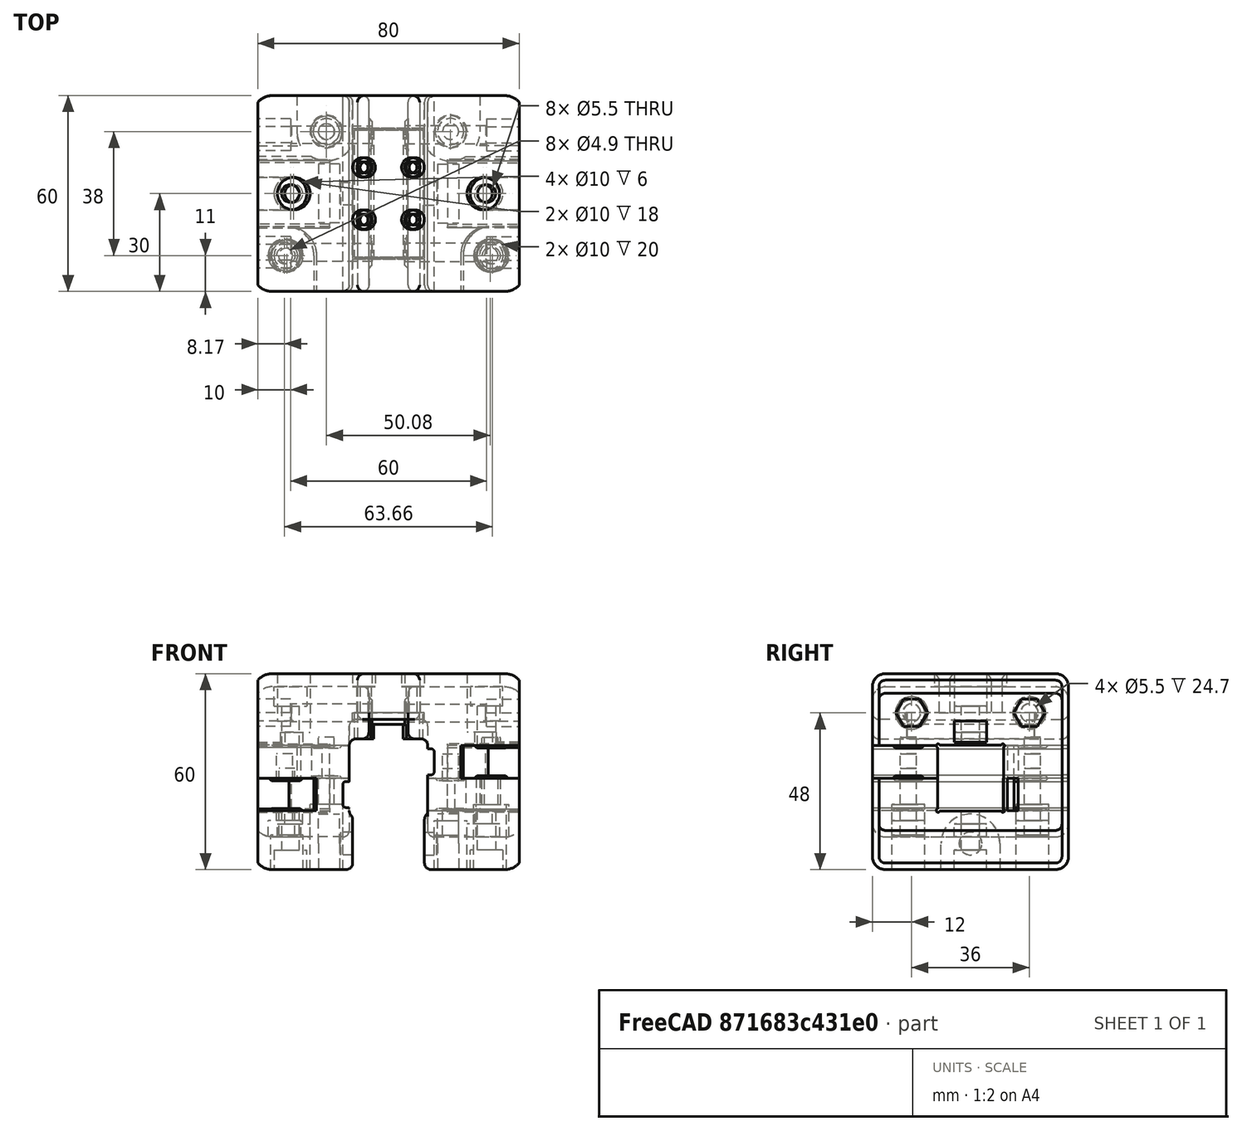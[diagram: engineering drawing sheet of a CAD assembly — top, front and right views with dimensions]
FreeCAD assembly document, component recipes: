
FREECAD ASSEMBLY — COMPONENT RECIPES ("y-carriages")

This assembly document has 7 components, labeled P0..P6 below (a component is one placed body or linked part). 7 of them carry a construction recipe — the FreeCAD feature program that regenerates the part from scratch, quoted from this document or its linked companion documents; the rest are supplied as boundary geometry only. No exploded tour is included for this assembly.
COMPONENT P0 — recipe-attached ("y-carriage-rail-drv", modeled in this document).
Construction recipe (the document's own serialized feature program — sketch geometry with constraints, then the solid features built on it; lengths are millimeters unless a unit is written):

FEATURE [Sketcher::SketchObject] Sketch
  ArcFitTolerance = 1e-06
  AttachmentSupport = -> [YZ_Plane257]
  FullyConstrained = true
  MakeInternals = false
  MapMode = 5
  Placement = pos=(0,0,0) rot=(0.57735,0.57735,0.57735;2.0944rad)
  sketch-geometry (18):
    g0: LineSegment StartX=-30 StartY=28 StartZ=0 EndX=-30 EndY=-14 EndZ=0
    g1: LineSegment StartX=-26 StartY=-18 StartZ=0 EndX=26 EndY=-18 EndZ=0
    g2: LineSegment StartX=30 StartY=-14 StartZ=0 EndX=30 EndY=28 EndZ=0
    g3: LineSegment StartX=26 StartY=32 StartZ=0 EndX=-26 EndY=32 EndZ=0
    g4: ArcOfCircle CenterX=26 CenterY=28 CenterZ=0 NormalX=0 NormalY=0 NormalZ=1 AngleXU=0 Radius=4 StartAngle=0 EndAngle=1.5708
    g5: GeomPoint [constr] X=30 Y=32 Z=0
    g6: ArcOfCircle CenterX=26 CenterY=-14 CenterZ=0 NormalX=0 NormalY=0 NormalZ=1 AngleXU=0 Radius=4 StartAngle=4.71239 EndAngle=6.28319
    g7: GeomPoint [constr] X=30 Y=-18 Z=0
    g8: ArcOfCircle CenterX=-26 CenterY=-14 CenterZ=0 NormalX=0 NormalY=0 NormalZ=1 AngleXU=0 Radius=4 StartAngle=3.14159 EndAngle=4.71239
    g9: GeomPoint [constr] X=-30 Y=-18 Z=0
    g10: ArcOfCircle CenterX=-26 CenterY=28 CenterZ=0 NormalX=0 NormalY=0 NormalZ=1 AngleXU=0 Radius=4 StartAngle=1.5708 EndAngle=3.14159
    g11: GeomPoint [constr] X=-30 Y=32 Z=0
    g12: LineSegment [constr] StartX=-10 StartY=10 StartZ=0 EndX=-10 EndY=-10 EndZ=0
    g13: LineSegment [constr] StartX=-10 StartY=-10 StartZ=0 EndX=10 EndY=-10 EndZ=0
    g14: LineSegment [constr] StartX=10 StartY=-10 StartZ=0 EndX=10 EndY=10 EndZ=0
    g15: LineSegment [constr] StartX=10 StartY=10 StartZ=0 EndX=-10 EndY=10 EndZ=0
    g16: GeomPoint [constr] X=0 Y=20 Z=0
    g17: GeomPoint [constr] X=0 Y=32 Z=0
  constraints (42):
    c: Vertical(g0)
    c: Vertical(g2)
    c: Horizontal(g1)
    c: Symmetric(g5,g11,g-2)
    c: PointOnObject(g5,g2)
    c: PointOnObject(g5,g3)
    c: Tangent(g2,g4) = -1.5708
    c: Tangent(g3,g4) = -1.5708
    c: PointOnObject(g7,g1)
    c: PointOnObject(g7,g2)
    c: Tangent(g1,g6) = -1.5708
    c: Tangent(g2,g6) = -1.5708
    c: PointOnObject(g9,g0)
    c: PointOnObject(g9,g1)
    c: Tangent(g0,g8) = -1.5708
    c: Tangent(g1,g8) = -1.5708
    c: PointOnObject(g11,g0)
    c: PointOnObject(g11,g3)
    c: Tangent(g0,g10) = -1.5708
    c: Tangent(g3,g10) = -1.5708
    c: Equal(g10,g4)
    c: Equal(g4,g6)
    c: Equal(g6,g8)
    c: Radius(g8) = 4
    c: Coincident(g12,g13)
    c: Coincident(g13,g14)
    c: Coincident(g14,g15)
    c: Coincident(g15,g12)
    c: Vertical(g12)
    c: Vertical(g14)
    c: Horizontal(g13)
    c: Horizontal(g15)
    c: Symmetric(g13,g12,g-1)
    c: Equal(g14,g15)
    c: DistanceX(g15,g15) = 20
    c: DistanceY(g7,g13) = 8
    c: DistanceX(g11,g5) = 60
    c: PointOnObject(g16,g-2)
    c: DistanceY(g16) = 20
    c: PointOnObject(g17,g3)
    c: PointOnObject(g17,g-2)
    c: DistanceY(g16,g17) = 12
FEATURE [PartDesign::Pad] Pad
  Direction = (1,0,0)
  Length = 40
  Length2 = 9.5
  Placement = pos=(0,0,0) rot=(1,1,1;2.0944rad)
  Profile = -> Sketch
  ReferenceAxis = -> Sketch [N_Axis]
  Suppressed = false
  Type = 4
FEATURE [Sketcher::SketchObject] Sketch469
  ArcFitTolerance = 0
  AttachmentOffset = pos=(0,0,18) rot=(0,0,1;0rad)
  AttachmentSupport = -> [YZ_Plane257]
  FullyConstrained = true
  MakeInternals = false
  MapMode = 5
  Placement = pos=(18,0,0) rot=(0.57735,0.57735,0.57735;2.0944rad)
  sketch-geometry (20):
    g0: LineSegment StartX=-9.4043 StartY=10.1 StartZ=0 EndX=9.4043 EndY=10.1 EndZ=0
    g1: LineSegment StartX=10.1 StartY=9.4043 StartZ=0 EndX=10.1 EndY=-9.4043 EndZ=0
    g2: LineSegment StartX=9.4043 StartY=-10.1 StartZ=0 EndX=-9.4043 EndY=-10.1 EndZ=0
    g3: LineSegment StartX=-10.1 StartY=-9.4043 StartZ=0 EndX=-10.1 EndY=9.4043 EndZ=0
    g4: ArcOfCircle CenterX=-9.92607 CenterY=9.92607 CenterZ=0 NormalX=0 NormalY=0 NormalZ=1 AngleXU=0 Radius=0.55 StartAngle=0.321751 EndAngle=4.39064
    g5: ArcOfCircle CenterX=9.92607 CenterY=9.92607 CenterZ=0 NormalX=0 NormalY=0 NormalZ=1 AngleXU=0 Radius=0.55 StartAngle=5.03414 EndAngle=9.10303
    g6: ArcOfCircle CenterX=9.92607 CenterY=-9.92607 CenterZ=0 NormalX=0 NormalY=0 NormalZ=1 AngleXU=0 Radius=0.55 StartAngle=3.46334 EndAngle=7.53223
    g7: ArcOfCircle CenterX=-9.92607 CenterY=-9.92607 CenterZ=0 NormalX=0 NormalY=0 NormalZ=1 AngleXU=0 Radius=0.55 StartAngle=1.89255 EndAngle=5.96143
    g8: LineSegment [constr] StartX=-10.1 StartY=9.4043 StartZ=0 EndX=-9.4043 EndY=10.1 EndZ=0
    g9: LineSegment [constr] StartX=9.4043 StartY=10.1 StartZ=0 EndX=10.1 EndY=9.4043 EndZ=0
    g10: LineSegment [constr] StartX=9.4043 StartY=-10.1 StartZ=0 EndX=10.1 EndY=-9.4043 EndZ=0
    g11: LineSegment [constr] StartX=-10.1 StartY=-9.4043 StartZ=0 EndX=-9.4043 EndY=-10.1 EndZ=0
    g12: GeomPoint [constr] X=-10.1 Y=10.1 Z=0
    g13: GeomPoint [constr] X=-9.75215 Y=9.75215 Z=0
    g14: GeomPoint [constr] X=9.75215 Y=9.75215 Z=0
    g15: GeomPoint [constr] X=10.1 Y=10.1 Z=0
    g16: GeomPoint [constr] X=-10.1 Y=-10.1 Z=0
    g17: GeomPoint [constr] X=-9.75215 Y=-9.75215 Z=0
    g18: GeomPoint [constr] X=10.1 Y=-10.1 Z=0
    g19: GeomPoint [constr] X=9.75215 Y=-9.75215 Z=0
  constraints (43):
    c: Horizontal(g0)
    c: Horizontal(g2)
    c: Vertical(g1)
    c: Vertical(g3)
    c: Coincident(g0,g4)
    c: Coincident(g3,g4)
    c: Coincident(g1,g5)
    c: Coincident(g0,g5)
    c: Coincident(g2,g6)
    c: Coincident(g1,g6)
    c: Coincident(g2,g7)
    c: Coincident(g3,g7)
    c: Coincident(g8,g3)
    c: Coincident(g8,g0)
    c: Coincident(g9,g0)
    c: Coincident(g9,g1)
    c: Coincident(g10,g2)
    c: Coincident(g10,g1)
    c: Coincident(g11,g3)
    c: Coincident(g11,g2)
    c: Equal(g6,g7)
    c: Equal(g7,g4)
    c: Equal(g4,g5)
    c: Parallel(g8,g10)
    c: Parallel(g11,g9)
    c: Perpendicular(g10,g9)
    c: Angle(g10) = 0.785398
    c: Radius(g4) = 0.55
    c: PointOnObject(g12,g0)
    c: Symmetric(g3,g0,g13)
    c: Symmetric(g13,g12,g4)
    c: Symmetric(g1,g0,g14)
    c: PointOnObject(g15,g1)
    c: Symmetric(g14,g15,g5)
    c: Symmetric(g3,g2,g17)
    c: PointOnObject(g16,g2)
    c: Symmetric(g16,g17,g7)
    c: PointOnObject(g18,g1)
    c: Symmetric(g18,g19,g6)
    c: Symmetric(g2,g1,g19)
    c: Symmetric(g18,g12,g-1)
    c: DistanceX(g16,g18) = 20.2
    c: DistanceY(g16,g12) = 20.2
FEATURE [PartDesign::Pocket] Pocket
  BaseFeature = -> Pad
  Direction = (-1,0,0)
  Length = 5
  Length2 = 5
  Placement = pos=(0,0,0) rot=(1,1,1;2.0944rad)
  Profile = -> Sketch469
  ReferenceAxis = -> Sketch469 [N_Axis]
  Reversed = true
  Suppressed = false
  Type = 1
FEATURE [Sketcher::SketchObject] Sketch470
  ArcFitTolerance = 1e-06
  AttachmentSupport = -> [XZ_Plane257]
  FullyConstrained = true
  MakeInternals = false
  MapMode = 5
  Placement = pos=(0,0,0) rot=(1,0,0;1.5708rad)
  sketch-geometry (10):
    g0: LineSegment [constr] StartX=-10 StartY=10 StartZ=0 EndX=-10 EndY=-10 EndZ=0
    g1: LineSegment [constr] StartX=-10 StartY=-10 StartZ=0 EndX=10 EndY=-10 EndZ=0
    g2: LineSegment [constr] StartX=10 StartY=-10 StartZ=0 EndX=10 EndY=10 EndZ=0
    g3: LineSegment [constr] StartX=10 StartY=10 StartZ=0 EndX=-10 EndY=10 EndZ=0
    g4: LineSegment StartX=-10 StartY=18 StartZ=0 EndX=-10 EndY=-28 EndZ=0
    g5: LineSegment StartX=-10 StartY=-28 StartZ=0 EndX=12 EndY=-28 EndZ=0
    g6: LineSegment StartX=12 StartY=-28 StartZ=0 EndX=12 EndY=16 EndZ=0
    g7: LineSegment StartX=10 StartY=18 StartZ=0 EndX=-10 EndY=18 EndZ=0
    g8: ArcOfCircle CenterX=10 CenterY=16 CenterZ=0 NormalX=0 NormalY=0 NormalZ=1 AngleXU=0 Radius=2 StartAngle=0 EndAngle=1.5708
    g9: GeomPoint [constr] X=12 Y=18 Z=0
  constraints (27):
    c: Coincident(g0,g1)
    c: Coincident(g1,g2)
    c: Coincident(g2,g3)
    c: Coincident(g3,g0)
    c: Vertical(g0)
    c: Vertical(g2)
    c: Horizontal(g1)
    c: Horizontal(g3)
    c: Symmetric(g1,g0,g-1)
    c: Equal(g2,g3)
    c: DistanceX(g3,g3) = 20
    c: Coincident(g4,g5)
    c: Coincident(g5,g6)
    c: Coincident(g7,g4)
    c: Vertical(g4)
    c: Vertical(g6)
    c: Horizontal(g5)
    c: Horizontal(g7)
    c: DistanceX(g2,g9) = 2
    c: PointOnObject(g0,g4)
    c: DistanceY(g5) = -28
    c: DistanceY(g2,g9) = 8
    c: PointOnObject(g9,g6)
    c: PointOnObject(g9,g7)
    c: Tangent(g6,g8) = -1.5708
    c: Tangent(g7,g8) = -1.5708
    c: Radius(g8) = 2
FEATURE [PartDesign::Pocket] Pocket181
  BaseFeature = -> Pocket
  Direction = (0,1,-2e-16)
  Length = 5
  Length2 = 5
  Midplane = true
  Placement = pos=(0,0,0) rot=(1,1,1;2.0944rad)
  Profile = -> Sketch470
  ReferenceAxis = -> Sketch470 [N_Axis]
  Suppressed = false
  Type = 1
FEATURE [Sketcher::SketchObject] Sketch471
  ArcFitTolerance = 1e-06
  AttachmentSupport = -> [XZ_Plane257]
  FullyConstrained = true
  MakeInternals = false
  MapMode = 5
  Placement = pos=(0,0,0) rot=(1,0,0;1.5708rad)
  sketch-geometry (4):
    g0: LineSegment StartX=-11 StartY=20 StartZ=0 EndX=-11 EndY=0 EndZ=0
    g1: LineSegment StartX=-11 StartY=0 StartZ=0 EndX=11 EndY=0 EndZ=0
    g2: LineSegment StartX=11 StartY=0 StartZ=0 EndX=11 EndY=20 EndZ=0
    g3: LineSegment StartX=11 StartY=20 StartZ=0 EndX=-11 EndY=20 EndZ=0
  constraints (11):
    c: Coincident(g0,g1)
    c: Coincident(g1,g2)
    c: Coincident(g2,g3)
    c: Coincident(g3,g0)
    c: Vertical(g0)
    c: Vertical(g2)
    c: Horizontal(g1)
    c: Symmetric(g2,g0,g-2)
    c: DistanceX(g3,g3) = 22
    c: DistanceY(g2) = 20
    c: PointOnObject(g1,g-1)
FEATURE [PartDesign::Pocket] Pocket182
  BaseFeature = -> Pocket181
  Direction = (0,1,-2e-16)
  Length = 40
  Length2 = 5
  Midplane = true
  Placement = pos=(0,0,0) rot=(1,1,1;2.0944rad)
  Profile = -> Sketch471
  ReferenceAxis = -> Sketch471 [N_Axis]
  Suppressed = false
  Type = 0
FEATURE [Sketcher::SketchObject] Sketch472
  ArcFitTolerance = 1e-06
  AttachmentOffset = pos=(8,0,8) rot=(0,0,1;0rad)
  AttachmentSupport = -> [YZ_Plane257]
  FullyConstrained = true
  MakeInternals = false
  MapMode = 5
  Placement = pos=(8,8,0) rot=(0.57735,0.57735,0.57735;2.0944rad)
  sketch-geometry (6):
    g0: LineSegment StartX=0 StartY=32 StartZ=0 EndX=3 EndY=32 EndZ=0
    g1: LineSegment StartX=3 StartY=32 StartZ=0 EndX=3 EndY=28 EndZ=0
    g2: LineSegment StartX=3 StartY=28 StartZ=0 EndX=1.7 EndY=28 EndZ=0
    g3: LineSegment StartX=1.7 StartY=28 StartZ=0 EndX=1.7 EndY=20 EndZ=0
    g4: LineSegment StartX=1.7 StartY=20 StartZ=0 EndX=0 EndY=20 EndZ=0
    g5: LineSegment StartX=0 StartY=20 StartZ=0 EndX=0 EndY=32 EndZ=0
  constraints (18):
    c: PointOnObject(g0,g-2)
    c: Horizontal(g0)
    c: Coincident(g0,g1)
    c: Vertical(g1)
    c: Coincident(g1,g2)
    c: Horizontal(g2)
    c: Coincident(g2,g3)
    c: Vertical(g3)
    c: Coincident(g3,g4)
    c: PointOnObject(g4,g-2)
    c: Horizontal(g4)
    c: Coincident(g4,g5)
    c: Coincident(g5,g0)
    c: DistanceY(g4) = 20
    c: DistanceX(g4,g4) = 1.7
    c: DistanceY(g3,g3) = 8
    c: DistanceX(g0,g0) = 3
    c: DistanceY(g0) = 32
FEATURE [PartDesign::Groove] Groove
  Angle = 360
  Angle2 = 60
  Axis = (0,0,1)
  Base = (8,8,0)
  BaseFeature = -> Pocket182
  Placement = pos=(0,0,0) rot=(1,1,1;2.0944rad)
  Profile = -> Sketch472
  ReferenceAxis = -> Sketch472 [V_Axis]
  Suppressed = false
  Type = 0
FEATURE [PartDesign::LinearPattern] LinearPattern
  Direction = -> X_Axis258
  Length = 15
  Mode = 0
  Occurrences = 2
  Offset = 15
  Placement = pos=(0,0,0) rot=(1,1,1;2.0944rad)
  Reversed = true
  Suppressed = false
  TransformMode = 0
FEATURE [PartDesign::Mirrored] Mirrored
  MirrorPlane = -> XZ_Plane257
  Placement = pos=(0,0,0) rot=(1,1,1;2.0944rad)
  Suppressed = false
  TransformMode = 0
FEATURE [PartDesign::MultiTransform] MultiTransform
  BaseFeature = -> Groove
  Originals = -> [Groove]
  Placement = pos=(0,0,0) rot=(1,1,1;2.0944rad)
  Suppressed = false
  TransformMode = 0
  Transformations = -> [LinearPattern,Mirrored]
FEATURE [Sketcher::SketchObject] Sketch473
  ArcFitTolerance = 1e-06
  AttachmentOffset = pos=(29,0,0) rot=(0,0,1;0rad)
  AttachmentSupport = -> [XZ_Plane257]
  FullyConstrained = true
  MakeInternals = false
  MapMode = 5
  Placement = pos=(29,0,0) rot=(1,0,0;1.5708rad)
  sketch-geometry (6):
    g0: LineSegment StartX=0 StartY=10 StartZ=0 EndX=0 EndY=32 EndZ=0
    g1: LineSegment StartX=0 StartY=32 StartZ=0 EndX=5 EndY=32 EndZ=0
    g2: LineSegment StartX=5 StartY=32 StartZ=0 EndX=5 EndY=14 EndZ=0
    g3: LineSegment StartX=5 StartY=14 StartZ=0 EndX=2.75 EndY=14 EndZ=0
    g4: LineSegment StartX=2.75 StartY=14 StartZ=0 EndX=2.75 EndY=10 EndZ=0
    g5: LineSegment StartX=2.75 StartY=10 StartZ=0 EndX=0 EndY=10 EndZ=0
  constraints (18):
    c: Vertical(g0)
    c: Coincident(g0,g1)
    c: Horizontal(g1)
    c: Coincident(g1,g2)
    c: Vertical(g2)
    c: Coincident(g2,g3)
    c: Horizontal(g3)
    c: Coincident(g3,g4)
    c: Vertical(g4)
    c: Coincident(g4,g5)
    c: Coincident(g5,g0)
    c: Horizontal(g5)
    c: DistanceY(g4,g4) = 4
    c: DistanceX(g1,g1) = 5
    c: DistanceY(g0) = 10
    c: DistanceX(g5,g5) = 2.75
    c: DistanceY(g1) = 32
    c: PointOnObject(g0,g-2)
FEATURE [PartDesign::Groove] Groove011
  Angle = 360
  Angle2 = 60
  Axis = (0,2e-16,1)
  Base = (29,0,0)
  BaseFeature = -> MultiTransform
  Placement = pos=(0,0,0) rot=(1,1,1;2.0944rad)
  Profile = -> Sketch473
  ReferenceAxis = -> Sketch473 [V_Axis]
  Suppressed = false
  Type = 0
FEATURE [PartDesign::Mirrored] Mirrored032
  BaseFeature = -> Groove011
  MirrorPlane = -> XY_Plane257
  Originals = -> [Groove011]
  Placement = pos=(0,0,0) rot=(1,1,1;2.0944rad)
  Suppressed = false
  TransformMode = 0
FEATURE [PartDesign::Chamfer] Chamfer
  Angle = 45
  Base = -> Mirrored032 [Edge40]
  BaseFeature = -> Mirrored032
  ChamferType = 0
  FlipDirection = false
  Placement = pos=(0,0,0) rot=(1,1,1;2.0944rad)
  Size = 2
  Size2 = 1
  SupportTransform = false
  Suppressed = false
  UseAllEdges = false
FEATURE [PartDesign::Fillet] Fillet002
  Base = -> Chamfer [Edge70]
  BaseFeature = -> Chamfer
  Placement = pos=(0,0,0) rot=(1,1,1;2.0944rad)
  Radius = 6
  SupportTransform = false
  Suppressed = false
  UseAllEdges = false
FEATURE [PartDesign::Fillet] Fillet003
  Base = -> Fillet002 [Edge3,Edge6,Edge33,Edge29,Edge28,Edge38]
  BaseFeature = -> Fillet002
  Placement = pos=(0,0,0) rot=(1,1,1;2.0944rad)
  Radius = 2
  SupportTransform = false
  Suppressed = false
  UseAllEdges = false
FEATURE [Sketcher::SketchObject] Sketch488
  ArcFitTolerance = 1e-06
  AttachmentSupport = -> [XZ_Plane257]
  FullyConstrained = true
  MakeInternals = false
  MapMode = 5
  Placement = pos=(0,0,0) rot=(1,0,0;1.5708rad)
  sketch-geometry (6):
    g0: LineSegment StartX=40 StartY=11 StartZ=0 EndX=33 EndY=11 EndZ=0
    g1: LineSegment StartX=33 StartY=11 StartZ=0 EndX=33 EndY=14 EndZ=0
    g2: LineSegment StartX=33 StartY=14 StartZ=0 EndX=29 EndY=14 EndZ=0
    g3: LineSegment StartX=29 StartY=14 StartZ=0 EndX=29 EndY=17.5 EndZ=0
    g4: LineSegment StartX=29 StartY=17.5 StartZ=0 EndX=40 EndY=17.5 EndZ=0
    g5: LineSegment StartX=40 StartY=17.5 StartZ=0 EndX=40 EndY=11 EndZ=0
  constraints (18):
    c: Horizontal(g0)
    c: Coincident(g0,g1)
    c: Vertical(g1)
    c: Coincident(g1,g2)
    c: Horizontal(g2)
    c: Coincident(g2,g3)
    c: Vertical(g3)
    c: Coincident(g3,g4)
    c: Horizontal(g4)
    c: Coincident(g4,g5)
    c: Coincident(g5,g0)
    c: Vertical(g5)
    c: DistanceX(g4) = 40
    c: DistanceY(g0) = 11
    c: DistanceY(g5,g5) = 6.5
    c: DistanceX(g0,g0) = 7
    c: DistanceY(g1,g1) = 3
    c: DistanceX(g2) = 29
FEATURE [PartDesign::Pocket] Pocket189
  BaseFeature = -> Fillet003
  Direction = (0,1,-2e-16)
  Length = 10
  Length2 = 5
  Midplane = true
  Placement = pos=(0,0,0) rot=(1,1,1;2.0944rad)
  Profile = -> Sketch488
  ReferenceAxis = -> Sketch488 [N_Axis]
  Refine = true
  Suppressed = false
  Type = 0
FEATURE [PartDesign::Body] Body  label="y-carriage-rail-drv"
  AllowCompound = false
  Group = -> [Sketch,Pad,Sketch469,Pocket,Sketch470,Pocket181,Sketch471,Pocket182,Sketch472,Groove,MultiTransform,LinearPattern,Mirrored,Sketch473,Groove011,Mirrored032,Chamfer,Fillet002,Fillet003,Sketch488,Pocket189]
  Origin = -> Origin258
  Tip = -> Pocket189
COMPONENT P1 — recipe-attached ("y-carriage-vslot-drv", modeled in this document).
Construction recipe (the document's own serialized feature program — sketch geometry with constraints, then the solid features built on it; lengths are millimeters unless a unit is written):

FEATURE [Sketcher::SketchObject] Sketch014
  ArcFitTolerance = 0
  AttachmentOffset = pos=(0,0,15) rot=(0,0,1;0rad)
  AttachmentSupport = -> [YZ_Plane251]
  FullyConstrained = true
  MakeInternals = false
  MapMode = 5
  Placement = pos=(15,0,0) rot=(0.57735,0.57735,0.57735;2.0944rad)
  sketch-geometry (5):
    g0: LineSegment StartX=9 StartY=-20 StartZ=0 EndX=9 EndY=-28 EndZ=0
    g1: LineSegment StartX=9 StartY=-28 StartZ=0 EndX=-9 EndY=-28 EndZ=0
    g2: LineSegment StartX=-9 StartY=-28 StartZ=0 EndX=-9 EndY=-20 EndZ=0
    g3: Circle [constr] CenterX=-5e-16 CenterY=-20 CenterZ=0 NormalX=0 NormalY=0 NormalZ=1 AngleXU=0 Radius=9
    g4: ArcOfCircle CenterX=-5e-16 CenterY=-20 CenterZ=0 NormalX=0 NormalY=0 NormalZ=1 AngleXU=0 Radius=9 StartAngle=0 EndAngle=3.14159
  constraints (12):
    c: Coincident(g0,g1)
    c: Coincident(g1,g2)
    c: Vertical(g0)
    c: Vertical(g2)
    c: Symmetric(g0,g1,g-2)
    c: DistanceY(g0) = -28
    c: DistanceX(g1,g1) = 18
    c: Diameter(g3) = 18
    c: DistanceY(g3) = -20
    c: Tangent(g0,g4) = 1.5708
    c: Tangent(g4,g2) = 1.5708
    c: Coincident(g4,g3)
FEATURE [Sketcher::SketchObject] Sketch015
  ArcFitTolerance = 0
  AttachmentOffset = pos=(0,0,14.7) rot=(0,0,1;0rad)
  AttachmentSupport = -> [YZ_Plane251]
  FullyConstrained = true
  MakeInternals = false
  MapMode = 5
  Placement = pos=(14.7,0,0) rot=(0.57735,0.57735,0.57735;2.0944rad)
  sketch-geometry (1):
    g0: Circle CenterX=0 CenterY=-20 CenterZ=0 NormalX=0 NormalY=0 NormalZ=1 AngleXU=0 Radius=3.5
  constraints (3):
    c: PointOnObject(g0,g-2)
    c: Diameter(g0) = 7
    c: DistanceY(g0) = -20
FEATURE [Sketcher::SketchObject] Sketch016
  ArcFitTolerance = 0
  AttachmentOffset = pos=(0,0,19) rot=(0,0,1;0rad)
  AttachmentSupport = -> [XZ_Plane251]
  FullyConstrained = true
  MakeInternals = false
  MapMode = 5
  Placement = pos=(0,-19,4.2e-15) rot=(1,0,0;1.5708rad)
  sketch-geometry (10):
    g0: GeomPoint [constr] X=31.83 Y=0.25 Z=0
    g1: GeomPoint [constr] X=31.83 Y=5 Z=0
    g2: LineSegment StartX=31.83 StartY=0.25 StartZ=0 EndX=31.83 EndY=0.75 EndZ=0
    g3: LineSegment StartX=31.83 StartY=0.75 StartZ=0 EndX=35.83 EndY=0.75 EndZ=0
    g4: LineSegment StartX=35.83 StartY=0.75 StartZ=0 EndX=36.33 EndY=0.25 EndZ=0
    g5: LineSegment StartX=36.33 StartY=0.25 StartZ=0 EndX=31.83 EndY=0.25 EndZ=0
    g6: LineSegment StartX=31.83 StartY=9.75 StartZ=0 EndX=31.83 EndY=9.25 EndZ=0
    g7: LineSegment StartX=31.83 StartY=9.25 StartZ=0 EndX=35.83 EndY=9.25 EndZ=0
    g8: LineSegment StartX=35.83 StartY=9.25 StartZ=0 EndX=36.33 EndY=9.75 EndZ=0
    g9: LineSegment StartX=36.33 StartY=9.75 StartZ=0 EndX=31.83 EndY=9.75 EndZ=0
  constraints (26):
    c: Vertical(g1,g0)
    c: Coincident(g2,g0)
    c: Vertical(g2)
    c: Coincident(g2,g3)
    c: Horizontal(g3)
    c: Coincident(g3,g4)
    c: Coincident(g4,g5)
    c: Coincident(g5,g2)
    c: Horizontal(g5)
    c: Coincident(g6,g7)
    c: Horizontal(g7)
    c: Coincident(g7,g8)
    c: Coincident(g8,g9)
    c: Coincident(g9,g6)
    c: Vertical(g6)
    c: Horizontal(g9)
    c: Symmetric(g2,g6,g1)
    c: Equal(g2,g6)
    c: DistanceY(g-1,g1) = 5
    c: DistanceX(g1) = 31.83
    c: DistanceY(g2,g6) = 9.5
    c: DistanceY(g2,g2) = 0.5
    c: DistanceX(g3,g3) = 4
    c: Angle(g4) = -0.785398
    c: Perpendicular(g4,g8)
    c: Equal(g9,g5)
FEATURE [Sketcher::SketchObject] Sketch227
  ArcFitTolerance = 0
  AttachmentOffset = pos=(0,0,6) rot=(0,0,1;0rad)
  AttachmentSupport = -> [YZ_Plane251]
  FullyConstrained = true
  MakeInternals = false
  MapMode = 5
  Placement = pos=(6,0,0) rot=(0.57735,0.57735,0.57735;2.0944rad)
  sketch-geometry (12):
    g0: LineSegment StartX=-26 StartY=28 StartZ=0 EndX=26 EndY=28 EndZ=0
    g1: LineSegment StartX=30 StartY=24 StartZ=0 EndX=30 EndY=-24 EndZ=0
    g2: LineSegment StartX=26 StartY=-28 StartZ=0 EndX=-26 EndY=-28 EndZ=0
    g3: LineSegment StartX=-30 StartY=-24 StartZ=0 EndX=-30 EndY=24 EndZ=0
    g4: ArcOfCircle CenterX=-26 CenterY=24 CenterZ=0 NormalX=0 NormalY=0 NormalZ=1 AngleXU=0 Radius=4 StartAngle=1.5708 EndAngle=3.14159
    g5: GeomPoint [constr] X=-30 Y=28 Z=0
    g6: ArcOfCircle CenterX=26 CenterY=24 CenterZ=0 NormalX=0 NormalY=0 NormalZ=1 AngleXU=0 Radius=4 StartAngle=2.62e-14 EndAngle=1.5708
    g7: GeomPoint [constr] X=30 Y=28 Z=0
    g8: ArcOfCircle CenterX=26 CenterY=-24 CenterZ=0 NormalX=0 NormalY=0 NormalZ=1 AngleXU=0 Radius=4 StartAngle=4.71239 EndAngle=6.28319
    g9: GeomPoint [constr] X=30 Y=-28 Z=0
    g10: ArcOfCircle CenterX=-26 CenterY=-24 CenterZ=0 NormalX=0 NormalY=0 NormalZ=1 AngleXU=0 Radius=4 StartAngle=3.14159 EndAngle=4.71239
    g11: GeomPoint [constr] X=-30 Y=-28 Z=0
  constraints (27):
    c: Horizontal(g0)
    c: Horizontal(g2)
    c: Vertical(g1)
    c: Vertical(g3)
    c: Symmetric(g9,g5,g-1)
    c: DistanceY(g9,g7) = 56
    c: DistanceX(g11,g9) = 60
    c: PointOnObject(g5,g0)
    c: PointOnObject(g5,g3)
    c: Tangent(g0,g4) = 1.5708
    c: Tangent(g3,g4) = 1.5708
    c: PointOnObject(g7,g0)
    c: PointOnObject(g7,g1)
    c: Tangent(g0,g6) = 1.5708
    c: Tangent(g1,g6) = 1.5708
    c: PointOnObject(g9,g1)
    c: PointOnObject(g9,g2)
    c: Tangent(g1,g8) = 1.5708
    c: Tangent(g2,g8) = 1.5708
    c: PointOnObject(g11,g2)
    c: PointOnObject(g11,g3)
    c: Tangent(g2,g10) = 1.5708
    c: Tangent(g3,g10) = 1.5708
    c: Equal(g10,g4)
    c: Equal(g4,g6)
    c: Equal(g6,g8)
    c: Radius(g8) = 4
FEATURE [PartDesign::Pad] Pad057
  Direction = (1,0,0)
  Length = 34
  Length2 = 10
  Placement = pos=(0,0,0) rot=(1,1,1;2.0944rad)
  Profile = -> Sketch227
  ReferenceAxis = -> Sketch227 [N_Axis]
  Suppressed = false
  Type = 0
FEATURE [Sketcher::SketchObject] Sketch228
  ArcFitTolerance = 0
  AttachmentOffset = pos=(0,0,18) rot=(0,0,1;0rad)
  AttachmentSupport = -> [YZ_Plane251]
  FullyConstrained = true
  MakeInternals = false
  MapMode = 5
  Placement = pos=(18,0,0) rot=(0.57735,0.57735,0.57735;2.0944rad)
  sketch-geometry (20):
    g0: LineSegment StartX=-9.4043 StartY=10.1 StartZ=0 EndX=9.4043 EndY=10.1 EndZ=0
    g1: LineSegment StartX=10.1 StartY=9.4043 StartZ=0 EndX=10.1 EndY=-9.4043 EndZ=0
    g2: LineSegment StartX=9.4043 StartY=-10.1 StartZ=0 EndX=-9.4043 EndY=-10.1 EndZ=0
    g3: LineSegment StartX=-10.1 StartY=-9.4043 StartZ=0 EndX=-10.1 EndY=9.4043 EndZ=0
    g4: ArcOfCircle CenterX=-9.92607 CenterY=9.92607 CenterZ=0 NormalX=0 NormalY=0 NormalZ=1 AngleXU=0 Radius=0.55 StartAngle=0.321751 EndAngle=4.39064
    g5: ArcOfCircle CenterX=9.92607 CenterY=9.92607 CenterZ=0 NormalX=0 NormalY=0 NormalZ=1 AngleXU=0 Radius=0.55 StartAngle=5.03414 EndAngle=9.10303
    g6: ArcOfCircle CenterX=9.92607 CenterY=-9.92607 CenterZ=0 NormalX=0 NormalY=0 NormalZ=1 AngleXU=0 Radius=0.55 StartAngle=3.46334 EndAngle=7.53223
    g7: ArcOfCircle CenterX=-9.92607 CenterY=-9.92607 CenterZ=0 NormalX=0 NormalY=0 NormalZ=1 AngleXU=0 Radius=0.55 StartAngle=1.89255 EndAngle=5.96143
    g8: LineSegment [constr] StartX=-10.1 StartY=9.4043 StartZ=0 EndX=-9.4043 EndY=10.1 EndZ=0
    g9: LineSegment [constr] StartX=9.4043 StartY=10.1 StartZ=0 EndX=10.1 EndY=9.4043 EndZ=0
    g10: LineSegment [constr] StartX=9.4043 StartY=-10.1 StartZ=0 EndX=10.1 EndY=-9.4043 EndZ=0
    g11: LineSegment [constr] StartX=-10.1 StartY=-9.4043 StartZ=0 EndX=-9.4043 EndY=-10.1 EndZ=0
    g12: GeomPoint [constr] X=-10.1 Y=10.1 Z=0
    g13: GeomPoint [constr] X=-9.75215 Y=9.75215 Z=0
    g14: GeomPoint [constr] X=9.75215 Y=9.75215 Z=0
    g15: GeomPoint [constr] X=10.1 Y=10.1 Z=0
    g16: GeomPoint [constr] X=-10.1 Y=-10.1 Z=0
    g17: GeomPoint [constr] X=-9.75215 Y=-9.75215 Z=0
    g18: GeomPoint [constr] X=10.1 Y=-10.1 Z=0
    g19: GeomPoint [constr] X=9.75215 Y=-9.75215 Z=0
  constraints (43):
    c: Horizontal(g0)
    c: Horizontal(g2)
    c: Vertical(g1)
    c: Vertical(g3)
    c: Coincident(g0,g4)
    c: Coincident(g3,g4)
    c: Coincident(g1,g5)
    c: Coincident(g0,g5)
    c: Coincident(g2,g6)
    c: Coincident(g1,g6)
    c: Coincident(g2,g7)
    c: Coincident(g3,g7)
    c: Coincident(g8,g3)
    c: Coincident(g8,g0)
    c: Coincident(g9,g0)
    c: Coincident(g9,g1)
    c: Coincident(g10,g2)
    c: Coincident(g10,g1)
    c: Coincident(g11,g3)
    c: Coincident(g11,g2)
    c: Equal(g6,g7)
    c: Equal(g7,g4)
    c: Equal(g4,g5)
    c: Parallel(g8,g10)
    c: Parallel(g11,g9)
    c: Perpendicular(g10,g9)
    c: Angle(g10) = 0.785398
    c: Radius(g4) = 0.55
    c: PointOnObject(g12,g0)
    c: Symmetric(g3,g0,g13)
    c: Symmetric(g13,g12,g4)
    c: Symmetric(g1,g0,g14)
    c: PointOnObject(g15,g1)
    c: Symmetric(g14,g15,g5)
    c: Symmetric(g3,g2,g17)
    c: PointOnObject(g16,g2)
    c: Symmetric(g16,g17,g7)
    c: PointOnObject(g18,g1)
    c: Symmetric(g18,g19,g6)
    c: Symmetric(g2,g1,g19)
    c: Symmetric(g18,g12,g-1)
    c: DistanceX(g16,g18) = 20.2
    c: DistanceY(g16,g12) = 20.2
FEATURE [PartDesign::Pocket] Pocket138
  BaseFeature = -> Pad057
  Direction = (-1,0,0)
  Length = 20
  Length2 = 5
  Placement = pos=(0,0,0) rot=(1,1,1;2.0944rad)
  Profile = -> Sketch228
  ReferenceAxis = -> Sketch228 [N_Axis]
  Reversed = true
  Suppressed = false
  Type = 1
FEATURE [Sketcher::SketchObject] Sketch229
  ArcFitTolerance = 0
  AttachmentSupport = -> [XZ_Plane251]
  FullyConstrained = true
  MakeInternals = false
  MapMode = 5
  Placement = pos=(0,0,0) rot=(1,0,0;1.5708rad)
  sketch-geometry (8):
    g0: LineSegment StartX=-10 StartY=12 StartZ=0 EndX=10 EndY=12 EndZ=0
    g1: LineSegment StartX=12 StartY=10 StartZ=0 EndX=12 EndY=-10 EndZ=0
    g2: LineSegment StartX=-12 StartY=-30 StartZ=0 EndX=-12 EndY=10 EndZ=0
    g3: ArcOfCircle CenterX=10 CenterY=10 CenterZ=0 NormalX=0 NormalY=0 NormalZ=1 AngleXU=0 Radius=2 StartAngle=1.8e-15 EndAngle=1.5708
    g4: ArcOfCircle CenterX=10 CenterY=-10 CenterZ=0 NormalX=0 NormalY=0 NormalZ=1 AngleXU=0 Radius=2 StartAngle=5.23599 EndAngle=6.28319
    g5: ArcOfCircle CenterX=-10 CenterY=10 CenterZ=0 NormalX=0 NormalY=0 NormalZ=1 AngleXU=0 Radius=2 StartAngle=1.5708 EndAngle=3.14159
    g6: LineSegment StartX=-12 StartY=-30 StartZ=0 EndX=11 EndY=-30 EndZ=0
    g7: LineSegment StartX=11 StartY=-30 StartZ=0 EndX=11 EndY=-11.7321 EndZ=0
  constraints (21):
    c: Tangent(g0,g3) = 1.5708
    c: Tangent(g1,g3) = 1.5708
    c: Tangent(g1,g4) = 1.5708
    c: Tangent(g0,g5) = 1.5708
    c: Tangent(g2,g5) = 1.5708
    c: Equal(g5,g3)
    c: Equal(g3,g4)
    c: Radius(g3) = 2
    c: DistanceX(g5,g3) = 20
    c: Symmetric(g4,g5,g-1)
    c: Horizontal(g5,g3)
    c: Vertical(g4,g3)
    c: Vertical(g2)
    c: DistanceY(g2) = -30
    c: Coincident(g6,g2)
    c: Horizontal(g6)
    c: Coincident(g7,g6)
    c: Coincident(g7,g4)
    c: Vertical(g7)
    c: DistanceX(g6) = 11
    c: Equal(g1,g0)
FEATURE [PartDesign::Pocket] Pocket139
  BaseFeature = -> Pocket138
  Direction = (0,1,-2e-16)
  Length = 5
  Length2 = 5
  Midplane = true
  Placement = pos=(0,0,0) rot=(1,1,1;2.0944rad)
  Profile = -> Sketch229
  ReferenceAxis = -> Sketch229 [N_Axis]
  Suppressed = false
  Type = 1
FEATURE [Sketcher::SketchObject] Sketch230
  ArcFitTolerance = 0
  AttachmentOffset = pos=(0,0,5) rot=(0,0,1;0rad)
  AttachmentSupport = -> [XY_Plane251]
  FullyConstrained = true
  MakeInternals = false
  MapMode = 5
  Placement = pos=(0,0,5) rot=(0,0,1;0rad)
  sketch-geometry (5):
    g0: ArcOfCircle CenterX=31.83 CenterY=-19 CenterZ=0 NormalX=0 NormalY=0 NormalZ=1 AngleXU=0 Radius=9 StartAngle=1.5708 EndAngle=3.14159
    g1: LineSegment StartX=22.83 StartY=-19 StartZ=0 EndX=22.83 EndY=-30 EndZ=0
    g2: LineSegment StartX=22.83 StartY=-30 StartZ=0 EndX=40.83 EndY=-30 EndZ=0
    g3: LineSegment StartX=40.83 StartY=-30 StartZ=0 EndX=40.83 EndY=-10 EndZ=0
    g4: LineSegment StartX=40.83 StartY=-10 StartZ=0 EndX=31.83 EndY=-10 EndZ=0
  constraints (15):
    c: Diameter(g0) = 18
    c: Vertical(g1)
    c: Coincident(g2,g1)
    c: Horizontal(g2)
    c: Coincident(g3,g2)
    c: Vertical(g3)
    c: Coincident(g4,g3)
    c: Horizontal(g4)
    c: Tangent(g0,g1) = -1.5708
    c: Tangent(g0,g4) = -1.5708
    c: Tangent(g3,g0)
    c: DistanceY(g1) = -30
    c: DistanceX(g0) = 31.83
    c: DistanceY(g0) = -19
    c: DistanceX(g0) = 31.83
FEATURE [Sketcher::SketchObject] Sketch231
  ArcFitTolerance = 0
  AttachmentOffset = pos=(0,0,-5) rot=(0,0,1;0rad)
  AttachmentSupport = -> [XY_Plane251]
  FullyConstrained = true
  MakeInternals = false
  MapMode = 5
  Placement = pos=(0,0,-5) rot=(0,0,1;0rad)
  sketch-geometry (10):
    g0: ArcOfCircle CenterX=19 CenterY=19 CenterZ=0 NormalX=0 NormalY=0 NormalZ=1 AngleXU=0 Radius=9 StartAngle=3.14159 EndAngle=5.25009
    g1: LineSegment StartX=10 StartY=19 StartZ=0 EndX=10 EndY=30 EndZ=0
    g2: LineSegment StartX=10 StartY=30 StartZ=0 EndX=28 EndY=30 EndZ=0
    g3: LineSegment StartX=28 StartY=30 StartZ=0 EndX=28 EndY=19 EndZ=0
    g4: LineSegment StartX=23.6095 StartY=11.27 StartZ=0 EndX=40 EndY=11.27 EndZ=0
    g5: LineSegment StartX=40 StartY=11.27 StartZ=0 EndX=40 EndY=14.65 EndZ=0
    g6: LineSegment StartX=40 StartY=14.65 StartZ=0 EndX=26.8789 EndY=14.65 EndZ=0
    g7: ArcOfCircle CenterX=19 CenterY=19 CenterZ=0 NormalX=0 NormalY=0 NormalZ=1 AngleXU=0 Radius=9 StartAngle=5.77873 EndAngle=6.28319
    g8: GeomPoint [constr] X=19 Y=12.9 Z=0
    g9: Circle [constr] CenterX=19 CenterY=19 CenterZ=0 NormalX=0 NormalY=0 NormalZ=1 AngleXU=0 Radius=6.1
  constraints (27):
    c: Diameter(g0) = 18
    c: Vertical(g1)
    c: Coincident(g2,g1)
    c: Horizontal(g2)
    c: Coincident(g3,g2)
    c: Vertical(g3)
    c: DistanceY(g2) = 30
    c: Tangent(g0,g1) = 1.5708
    c: Horizontal(g4)
    c: Coincident(g5,g4)
    c: Vertical(g5)
    c: Coincident(g6,g5)
    c: Horizontal(g6)
    c: Equal(g0,g7)
    c: Coincident(g0,g4)
    c: Coincident(g7,g6)
    c: Coincident(g0,g7)
    c: Tangent(g7,g3) = 1.5708
    c: DistanceX(g5) = 40
    c: Vertical(g8,g0)
    c: DistanceY(g0,g8) = 1.63
    c: DistanceY(g8,g6) = 1.75
    c: Coincident(g9,g0)
    c: Diameter(g9) = 12.2
    c: PointOnObject(g8,g9)
    c: DistanceX(g0) = 19
    c: DistanceY(g0) = 19
FEATURE [Sketcher::SketchObject] Sketch232
  ArcFitTolerance = 0
  AttachmentOffset = pos=(0,0,29.7) rot=(0,0,1;0rad)
  AttachmentSupport = -> [YZ_Plane251]
  FullyConstrained = true
  MakeInternals = false
  MapMode = 5
  Placement = pos=(29.7,0,0) rot=(0.57735,0.57735,0.57735;2.0944rad)
  sketch-geometry (2):
    g0: Circle CenterX=18 CenterY=20 CenterZ=0 NormalX=0 NormalY=0 NormalZ=1 AngleXU=0 Radius=2.75
    g1: Circle CenterX=-18 CenterY=20 CenterZ=0 NormalX=0 NormalY=0 NormalZ=1 AngleXU=0 Radius=2.75
  constraints (5):
    c: Symmetric(g1,g0,g-2)
    c: Equal(g1,g0)
    c: Diameter(g1) = 5.5
    c: DistanceX(g1,g0) = 36
    c: DistanceY(g0) = 20
FEATURE [Sketcher::SketchObject] Sketch233
  ArcFitTolerance = 0
  AttachmentOffset = pos=(0,0,30) rot=(0,0,1;0rad)
  AttachmentSupport = -> [YZ_Plane251]
  FullyConstrained = true
  MakeInternals = false
  MapMode = 5
  Placement = pos=(30,0,0) rot=(0.57735,0.57735,0.57735;2.0944rad)
  sketch-geometry (14):
    g0: LineSegment StartX=-15.5751 StartY=15.8 StartZ=0 EndX=-13.1503 EndY=20 EndZ=0
    g1: LineSegment StartX=-13.1503 StartY=20 StartZ=0 EndX=-15.5751 EndY=24.2 EndZ=0
    g2: LineSegment StartX=-15.5751 StartY=24.2 StartZ=0 EndX=-20.4249 EndY=24.2 EndZ=0
    g3: LineSegment StartX=-20.4249 StartY=24.2 StartZ=0 EndX=-22.8497 EndY=20 EndZ=0
    g4: LineSegment StartX=-22.8497 StartY=20 StartZ=0 EndX=-20.4249 EndY=15.8 EndZ=0
    g5: LineSegment StartX=-20.4249 StartY=15.8 StartZ=0 EndX=-15.5751 EndY=15.8 EndZ=0
    g6: Circle [constr] CenterX=-18 CenterY=20 CenterZ=0 NormalX=0 NormalY=0 NormalZ=1 AngleXU=0 Radius=4.84974
    g7: LineSegment StartX=20.4249 StartY=15.8 StartZ=0 EndX=22.8497 EndY=20 EndZ=0
    g8: LineSegment StartX=22.8497 StartY=20 StartZ=0 EndX=20.4249 EndY=24.2 EndZ=0
    g9: LineSegment StartX=20.4249 StartY=24.2 StartZ=0 EndX=15.5751 EndY=24.2 EndZ=0
    g10: LineSegment StartX=15.5751 StartY=24.2 StartZ=0 EndX=13.1503 EndY=20 EndZ=0
    g11: LineSegment StartX=13.1503 StartY=20 StartZ=0 EndX=15.5751 EndY=15.8 EndZ=0
    g12: LineSegment StartX=15.5751 StartY=15.8 StartZ=0 EndX=20.4249 EndY=15.8 EndZ=0
    g13: Circle [constr] CenterX=18 CenterY=20 CenterZ=0 NormalX=0 NormalY=0 NormalZ=1 AngleXU=0 Radius=4.84974
  constraints (33):
    c: Coincident(g0,g1)
    c: Coincident(g1,g2)
    c: Coincident(g2,g3)
    c: Coincident(g3,g4)
    c: Coincident(g4,g5)
    c: Coincident(g5,g0)
    c: Equal(g0, g1-g5) x5
    c: PointOnObject(g0,g6)
    c: PointOnObject(g1,g6)
    c: PointOnObject(g2,g6)
    c: PointOnObject(g3,g6)
    c: PointOnObject(g4,g6)
    c: PointOnObject(g5,g6)
    c: Coincident(g7,g8)
    c: Coincident(g8,g9)
    c: Coincident(g9,g10)
    c: Coincident(g10,g11)
    c: Coincident(g11,g12)
    c: Coincident(g12,g7)
    c: Equal(g7, g8-g12) x5
    c: PointOnObject(g7,g13)
    c: PointOnObject(g8,g13)
    c: PointOnObject(g9,g13)
    c: PointOnObject(g10,g13)
    c: PointOnObject(g11,g13)
    c: PointOnObject(g12,g13)
    c: Horizontal(g9)
    c: Horizontal(g2)
    c: Symmetric(g6,g13,g-2)
    c: Equal(g13,g6)
    c: DistanceY(g6) = 20
    c: DistanceX(g6,g13) = 36
    c: DistanceY(g7,g8) = 8.4
FEATURE [Sketcher::SketchObject] Sketch234
  ArcFitTolerance = 0
  AttachmentOffset = pos=(0,0,20) rot=(0,0,1;0rad)
  AttachmentSupport = -> [XY_Plane251]
  FullyConstrained = true
  MakeInternals = false
  MapMode = 5
  Placement = pos=(0,0,20) rot=(0,0,1;0rad)
  sketch-geometry (5):
    g0: GeomPoint [constr] X=6 Y=18 Z=0
    g1: LineSegment StartX=6 StartY=18 StartZ=0 EndX=6 EndY=23 EndZ=0
    g2: LineSegment StartX=6 StartY=23 StartZ=0 EndX=5 EndY=22 EndZ=0
    g3: LineSegment StartX=5 StartY=22 StartZ=0 EndX=5 EndY=18 EndZ=0
    g4: LineSegment StartX=5 StartY=18 StartZ=0 EndX=6 EndY=18 EndZ=0
  constraints (13):
    c: DistanceX(g0) = 6
    c: DistanceY(g0) = 18
    c: Coincident(g1,g0)
    c: Vertical(g1)
    c: Coincident(g1,g2)
    c: Coincident(g2,g3)
    c: Vertical(g3)
    c: Coincident(g3,g4)
    c: Coincident(g4,g1)
    c: Horizontal(g4)
    c: Angle(g2) = -2.35619
    c: DistanceY(g3,g3) = 4
    c: DistanceX(g3) = 5
FEATURE [PartDesign::Revolution] Revolution016
  Angle = 360
  Angle2 = 60
  Axis = (1,0,0)
  Base = (5,18,20)
  BaseFeature = -> Pocket139
  Placement = pos=(0,0,0) rot=(1,1,1;2.0944rad)
  Profile = -> Sketch234
  ReferenceAxis = -> Sketch234 [Edge4]
  Reversed = true
  Suppressed = false
  Type = 0
FEATURE [PartDesign::Mirrored] Mirrored030
  BaseFeature = -> Revolution016
  MirrorPlane = -> XZ_Plane251
  Originals = -> [Revolution016]
  Placement = pos=(0,0,0) rot=(1,1,1;2.0944rad)
  Suppressed = false
  TransformMode = 0
FEATURE [PartDesign::Pocket] Pocket142
  BaseFeature = -> Mirrored030
  Direction = (-1,0,0)
  Length = 5
  Length2 = 5
  Placement = pos=(0,0,0) rot=(1,1,1;2.0944rad)
  Profile = -> Sketch232
  ReferenceAxis = -> Sketch232 [N_Axis]
  Suppressed = false
  Type = 1
FEATURE [PartDesign::Pocket] Pocket143
  BaseFeature = -> Pocket142
  Direction = (-1,0,0)
  Length = 5
  Length2 = 5
  Placement = pos=(0,0,0) rot=(1,1,1;2.0944rad)
  Profile = -> Sketch233
  ReferenceAxis = -> Sketch233 [N_Axis]
  Reversed = true
  Suppressed = false
  Type = 1
FEATURE [Sketcher::SketchObject] Sketch235
  ArcFitTolerance = 0
  AttachmentSupport = -> [XY_Plane251]
  FullyConstrained = true
  MakeInternals = false
  MapMode = 5
  sketch-geometry (1):
    g0: Circle CenterX=30 CenterY=0 CenterZ=0 NormalX=0 NormalY=0 NormalZ=1 AngleXU=0 Radius=2.75
  constraints (3):
    c: PointOnObject(g0,g-1)
    c: DistanceX(g0) = 30
    c: Diameter(g0) = 5.5
FEATURE [PartDesign::Pocket] Pocket144
  BaseFeature = -> Pocket143
  Direction = (0,0,-1)
  Length = 5
  Length2 = 5
  Midplane = true
  Placement = pos=(0,0,0) rot=(1,1,1;2.0944rad)
  Profile = -> Sketch235
  ReferenceAxis = -> Sketch235 [N_Axis]
  Suppressed = false
  Type = 1
FEATURE [Sketcher::SketchObject] Sketch236
  ArcFitTolerance = 0
  AttachmentOffset = pos=(0,0,22) rot=(0,0,1;0rad)
  AttachmentSupport = -> [XY_Plane251]
  FullyConstrained = true
  MakeInternals = false
  MapMode = 5
  Placement = pos=(0,0,22) rot=(0,0,1;0rad)
  sketch-geometry (1):
    g0: Circle CenterX=30 CenterY=0 CenterZ=0 NormalX=0 NormalY=0 NormalZ=1 AngleXU=0 Radius=5
  constraints (3):
    c: PointOnObject(g0,g-1)
    c: DistanceX(g0) = 30
    c: Diameter(g0) = 10
FEATURE [PartDesign::Pocket] Pocket145
  BaseFeature = -> Pocket144
  Direction = (0,0,-1)
  Length = 5
  Length2 = 5
  Placement = pos=(0,0,0) rot=(1,1,1;2.0944rad)
  Profile = -> Sketch236
  ReferenceAxis = -> Sketch236 [N_Axis]
  Reversed = true
  Suppressed = false
  Type = 1
FEATURE [PartDesign::Mirrored] Mirrored031
  BaseFeature = -> Pocket145
  MirrorPlane = -> XY_Plane251
  Originals = -> [Pocket145]
  Placement = pos=(0,0,0) rot=(1,1,1;2.0944rad)
  Suppressed = false
  TransformMode = 0
FEATURE [PartDesign::Pocket] Pocket146
  BaseFeature = -> Mirrored031
  Direction = (-1,0,0)
  Length = 6.5
  Length2 = 5
  Placement = pos=(0,0,0) rot=(1,1,1;2.0944rad)
  Profile = -> Sketch014
  ReferenceAxis = -> Sketch014 [N_Axis]
  Reversed = true
  Suppressed = false
  Type = 0
FEATURE [PartDesign::Pocket] Pocket009
  BaseFeature = -> Pocket146
  Direction = (-1,0,0)
  Length = 5
  Length2 = 5
  Placement = pos=(0,0,0) rot=(1,1,1;2.0944rad)
  Profile = -> Sketch015
  ReferenceAxis = -> Sketch015 [N_Axis]
  Suppressed = false
  Type = 1
FEATURE [PartDesign::Chamfer] Chamfer001
  Angle = 45
  Base = -> Pocket009 [Edge8]
  BaseFeature = -> Pocket009
  ChamferType = 0
  FlipDirection = false
  Placement = pos=(0,0,0) rot=(1,1,1;2.0944rad)
  Size = 2
  Size2 = 1
  SupportTransform = false
  Suppressed = false
  UseAllEdges = false
FEATURE [PartDesign::Fillet] Fillet
  Base = -> Chamfer001 [Edge2]
  BaseFeature = -> Chamfer001
  Placement = pos=(0,0,0) rot=(1,1,1;2.0944rad)
  Radius = 6
  SupportTransform = false
  Suppressed = false
  UseAllEdges = false
FEATURE [PartDesign::Fillet] Fillet001
  Base = -> Fillet [Edge9,Edge36,Edge16,Edge3,Edge6,Edge27]
  BaseFeature = -> Fillet
  Placement = pos=(0,0,0) rot=(1,1,1;2.0944rad)
  Radius = 2
  SupportTransform = false
  Suppressed = false
  UseAllEdges = false
FEATURE [Sketcher::SketchObject] Sketch237
  ArcFitTolerance = 0
  AttachmentOffset = pos=(0,0,19) rot=(0,0,1;0rad)
  AttachmentSupport = -> [XZ_Plane251]
  FullyConstrained = true
  MakeInternals = false
  MapMode = 5
  Placement = pos=(0,-19,4.2e-15) rot=(1,0,0;1.5708rad)
  sketch-geometry (6):
    g0: LineSegment StartX=31.83 StartY=12.5 StartZ=0 EndX=31.83 EndY=-28 EndZ=0
    g1: LineSegment StartX=31.83 StartY=-28 StartZ=0 EndX=26.83 EndY=-28 EndZ=0
    g2: LineSegment StartX=26.83 StartY=-28 StartZ=0 EndX=26.83 EndY=-8 EndZ=0
    g3: LineSegment StartX=26.83 StartY=-8 StartZ=0 EndX=29.38 EndY=-8 EndZ=0
    g4: LineSegment StartX=29.38 StartY=-8 StartZ=0 EndX=29.38 EndY=12.5 EndZ=0
    g5: LineSegment StartX=29.38 StartY=12.5 StartZ=0 EndX=31.83 EndY=12.5 EndZ=0
  constraints (18):
    c: Vertical(g0)
    c: Coincident(g0,g1)
    c: Horizontal(g1)
    c: Coincident(g1,g2)
    c: Vertical(g2)
    c: Coincident(g2,g3)
    c: Horizontal(g3)
    c: Coincident(g3,g4)
    c: Coincident(g4,g5)
    c: Coincident(g5,g0)
    c: Horizontal(g5)
    c: DistanceY(g4,g4) = 20.5
    c: DistanceX(g5,g5) = 2.45
    c: DistanceX(g0) = 31.83
    c: DistanceY(g0) = -28
    c: DistanceX(g1,g1) = 5
    c: DistanceY(g4) = 12.5
    c: Vertical(g4)
FEATURE [Sketcher::SketchObject] Sketch238
  ArcFitTolerance = 0
  AttachmentOffset = pos=(0,0,-19) rot=(0,0,1;0rad)
  AttachmentSupport = -> [XZ_Plane251]
  FullyConstrained = true
  MakeInternals = false
  MapMode = 5
  Placement = pos=(0,19,-4.2e-15) rot=(1,0,0;1.5708rad)
  sketch-geometry (6):
    g0: LineSegment StartX=19 StartY=3 StartZ=0 EndX=19 EndY=-28 EndZ=0
    g1: LineSegment StartX=19 StartY=-28 StartZ=0 EndX=14 EndY=-28 EndZ=0
    g2: LineSegment StartX=14 StartY=-28 StartZ=0 EndX=14 EndY=-17.5 EndZ=0
    g3: LineSegment StartX=14 StartY=-17.5 StartZ=0 EndX=16.55 EndY=-17.5 EndZ=0
    g4: LineSegment StartX=16.55 StartY=-17.5 StartZ=0 EndX=16.55 EndY=3 EndZ=0
    g5: LineSegment StartX=16.55 StartY=3 StartZ=0 EndX=19 EndY=3 EndZ=0
  constraints (18):
    c: Vertical(g0)
    c: Coincident(g0,g1)
    c: Horizontal(g1)
    c: Coincident(g1,g2)
    c: Vertical(g2)
    c: Coincident(g2,g3)
    c: Horizontal(g3)
    c: Coincident(g3,g4)
    c: Vertical(g4)
    c: Coincident(g4,g5)
    c: Coincident(g5,g0)
    c: Horizontal(g5)
    c: DistanceX(g5,g5) = 2.45
    c: DistanceX(g0) = 19
    c: DistanceX(g1,g1) = 5
    c: DistanceY(g0) = 3
    c: DistanceY(g4,g4) = 20.5
    c: DistanceY(g0) = -28
FEATURE [Sketcher::SketchObject] Sketch239
  ArcFitTolerance = 0
  AttachmentOffset = pos=(0,0,-19) rot=(0,0,1;0rad)
  AttachmentSupport = -> [XZ_Plane251]
  FullyConstrained = true
  MakeInternals = false
  MapMode = 5
  Placement = pos=(0,19,-4.2e-15) rot=(1,0,0;1.5708rad)
  sketch-geometry (9):
    g0: GeomPoint [constr] X=19 Y=-5 Z=0
    g1: LineSegment StartX=19 StartY=-0.25 StartZ=0 EndX=19 EndY=-0.75 EndZ=0
    g2: LineSegment StartX=19 StartY=-0.75 StartZ=0 EndX=23 EndY=-0.75 EndZ=0
    g3: LineSegment StartX=23 StartY=-0.75 StartZ=0 EndX=23.5 EndY=-0.25 EndZ=0
    g4: LineSegment StartX=23.5 StartY=-0.25 StartZ=0 EndX=19 EndY=-0.25 EndZ=0
    g5: LineSegment StartX=19 StartY=-9.75 StartZ=0 EndX=19 EndY=-9.25 EndZ=0
    g6: LineSegment StartX=19 StartY=-9.25 StartZ=0 EndX=23 EndY=-9.25 EndZ=0
    g7: LineSegment StartX=23 StartY=-9.25 StartZ=0 EndX=23.5 EndY=-9.75 EndZ=0
    g8: LineSegment StartX=23.5 StartY=-9.75 StartZ=0 EndX=19 EndY=-9.75 EndZ=0
  constraints (25):
    c: DistanceX(g0) = 19
    c: DistanceY(g0) = -5
    c: Vertical(g1)
    c: Coincident(g1,g2)
    c: Horizontal(g2)
    c: Coincident(g2,g3)
    c: Coincident(g3,g4)
    c: Coincident(g4,g1)
    c: Horizontal(g4)
    c: Vertical(g5)
    c: Coincident(g5,g6)
    c: Horizontal(g6)
    c: Coincident(g6,g7)
    c: Coincident(g7,g8)
    c: Coincident(g8,g5)
    c: Horizontal(g8)
    c: Symmetric(g5,g1,g0)
    c: Vertical(g5,g1)
    c: DistanceY(g5,g5) = 0.5
    c: Angle(g7) = -0.785398
    c: DistanceX(g6,g6) = 4
    c: Equal(g1,g5)
    c: Perpendicular(g7,g3)
    c: Equal(g2,g6)
    c: DistanceY(g5,g1) = 9.5
FEATURE [PartDesign::Body] Body118  label="y-carriage-vslot-drv"
  AllowCompound = false
  Group = -> [Sketch227,Pad057,Sketch228,Pocket138,Sketch229,Pocket139,Sketch230,Sketch231,Sketch232,Sketch233,Sketch234,Revolution016,Mirrored030,Pocket142,Pocket143,Sketch235,Pocket144,Sketch236,Pocket145,Mirrored031,Sketch014,Pocket146,Sketch015,Pocket009,Sketch016,Sketch237,Sketch238,Sketch239,Chamfer001,Fillet,Fillet001]
  Origin = -> Origin252
  Tip = -> Fillet001
COMPONENT P2 — recipe-attached ("carriage-mgn9h-drv", modeled in this document).
Construction recipe (the document's own serialized feature program — sketch geometry with constraints, then the solid features built on it; lengths are millimeters unless a unit is written):

FEATURE [Sketcher::SketchObject] Sketch468
  ArcFitTolerance = 1e-06
  AttachmentSupport = -> [XZ_Plane293]
  FullyConstrained = true
  MakeInternals = false
  MapMode = 5
  Placement = pos=(0,0,0) rot=(1,0,0;1.5708rad)
  sketch-geometry (8):
    g0: LineSegment StartX=-10 StartY=10 StartZ=0 EndX=-10 EndY=2 EndZ=0
    g1: LineSegment StartX=-10 StartY=2 StartZ=0 EndX=-5 EndY=2 EndZ=0
    g2: LineSegment StartX=10 StartY=2 StartZ=0 EndX=10 EndY=10 EndZ=0
    g3: LineSegment StartX=10 StartY=10 StartZ=0 EndX=-10 EndY=10 EndZ=0
    g4: LineSegment StartX=-5 StartY=2 StartZ=0 EndX=-5 EndY=6.5 EndZ=0
    g5: LineSegment StartX=-5 StartY=6.5 StartZ=0 EndX=5 EndY=6.5 EndZ=0
    g6: LineSegment StartX=5 StartY=6.5 StartZ=0 EndX=5 EndY=2 EndZ=0
    g7: LineSegment StartX=5 StartY=2 StartZ=0 EndX=10 EndY=2 EndZ=0
  constraints (23):
    c: Coincident(g0,g1)
    c: Coincident(g7,g2)
    c: Coincident(g2,g3)
    c: Coincident(g3,g0)
    c: Vertical(g0)
    c: Vertical(g2)
    c: Horizontal(g1)
    c: Symmetric(g2,g0,g-2)
    c: DistanceX(g3,g3) = 20
    c: DistanceY(g2) = 10
    c: DistanceY(g7) = 2
    c: Vertical(g4)
    c: Coincident(g4,g5)
    c: Coincident(g5,g6)
    c: PointOnObject(g6,g7)
    c: Vertical(g6)
    c: Coincident(g1,g4)
    c: PointOnObject(g7,g6)
    c: Symmetric(g5,g4,g-2)
    c: DistanceX(g5,g5) = 10
    c: DistanceY(g5) = 6.5
    c: Horizontal(g7)
    c: Horizontal(g1,g6)
FEATURE [PartDesign::Pad] Pad102
  Direction = (0,-1,2e-16)
  Length = 39
  Length2 = 10
  Midplane = true
  Placement = pos=(0,0,0) rot=(1,0,0;1.5708rad)
  Profile = -> Sketch468
  ReferenceAxis = -> Sketch468 [N_Axis]
  Suppressed = false
  Type = 0
FEATURE [PartDesign::Body] Body154  label="carriage-mgn9h-drv"
  AllowCompound = false
  Group = -> [Sketch468,Pad102]
  Origin = -> Origin294
  Tip = -> Pad102
COMPONENT P3 — recipe-attached ("main-vslot-left", modeled in this document).
Construction recipe (the document's own serialized feature program — sketch geometry with constraints, then the solid features built on it; lengths are millimeters unless a unit is written):

FEATURE [PartDesign::FeatureBase] Clone068
  BaseFeature = -> Body118
  Suppressed = false
FEATURE [Sketcher::SketchObject] Sketch242
  ArcFitTolerance = 0
  AttachmentOffset = pos=(0,0,19) rot=(0,0,1;0rad)
  AttachmentSupport = -> [XZ_Plane253]
  FullyConstrained = true
  MakeInternals = false
  MapMode = 5
  Placement = pos=(0,-19,4.2e-15) rot=(1,0,0;1.5708rad)
  sketch-geometry (10):
    g0: GeomPoint [constr] X=31.08 Y=-2e-16 Z=0
    g1: GeomPoint [constr] X=31.08 Y=5 Z=0
    g2: LineSegment StartX=31.08 StartY=-2e-16 StartZ=0 EndX=31.08 EndY=0.75 EndZ=0
    g3: LineSegment StartX=31.08 StartY=0.75 StartZ=0 EndX=35.08 EndY=0.75 EndZ=0
    g4: LineSegment StartX=35.08 StartY=0.75 StartZ=0 EndX=35.83 EndY=-2e-16 EndZ=0
    g5: LineSegment StartX=35.83 StartY=-2e-16 StartZ=0 EndX=31.08 EndY=-2e-16 EndZ=0
    g6: LineSegment StartX=31.08 StartY=10 StartZ=0 EndX=31.08 EndY=9.25 EndZ=0
    g7: LineSegment StartX=31.08 StartY=9.25 StartZ=0 EndX=35.08 EndY=9.25 EndZ=0
    g8: LineSegment StartX=35.08 StartY=9.25 StartZ=0 EndX=35.83 EndY=10 EndZ=0
    g9: LineSegment StartX=35.83 StartY=10 StartZ=0 EndX=31.08 EndY=10 EndZ=0
  constraints (26):
    c: Vertical(g1,g0)
    c: Coincident(g2,g0)
    c: Vertical(g2)
    c: Coincident(g2,g3)
    c: Horizontal(g3)
    c: Coincident(g3,g4)
    c: Coincident(g4,g5)
    c: Coincident(g5,g2)
    c: Horizontal(g5)
    c: Coincident(g6,g7)
    c: Horizontal(g7)
    c: Coincident(g7,g8)
    c: Coincident(g8,g9)
    c: Coincident(g9,g6)
    c: Vertical(g6)
    c: Horizontal(g9)
    c: Symmetric(g2,g6,g1)
    c: Equal(g2,g6)
    c: DistanceY(g-1,g1) = 5
    c: DistanceX(g1) = 31.08
    c: DistanceY(g2,g6) = 10
    c: DistanceX(g3,g3) = 4
    c: Angle(g4) = -0.785398
    c: Perpendicular(g4,g8)
    c: Equal(g9,g5)
    c: DistanceY(g2,g6) = 8.5
FEATURE [Sketcher::SketchObject] Sketch243
  ArcFitTolerance = 0
  AttachmentOffset = pos=(0,0,5) rot=(0,0,1;0rad)
  AttachmentSupport = -> [XY_Plane253]
  FullyConstrained = true
  MakeInternals = false
  MapMode = 5
  Placement = pos=(0,0,5) rot=(0,0,1;0rad)
  sketch-geometry (5):
    g0: ArcOfCircle CenterX=31.08 CenterY=-19 CenterZ=0 NormalX=0 NormalY=0 NormalZ=1 AngleXU=0 Radius=9 StartAngle=1.5708 EndAngle=3.14159
    g1: LineSegment StartX=22.08 StartY=-19 StartZ=0 EndX=22.08 EndY=-30 EndZ=0
    g2: LineSegment StartX=22.08 StartY=-30 StartZ=0 EndX=40.08 EndY=-30 EndZ=0
    g3: LineSegment StartX=40.08 StartY=-30 StartZ=0 EndX=40.08 EndY=-10 EndZ=0
    g4: LineSegment StartX=40.08 StartY=-10 StartZ=0 EndX=31.08 EndY=-10 EndZ=0
  constraints (14):
    c: Diameter(g0) = 18
    c: Vertical(g1)
    c: Coincident(g2,g1)
    c: Horizontal(g2)
    c: Coincident(g3,g2)
    c: Vertical(g3)
    c: Coincident(g4,g3)
    c: Horizontal(g4)
    c: Tangent(g0,g1) = -1.5708
    c: Tangent(g0,g4) = -1.5708
    c: Tangent(g3,g0)
    c: DistanceY(g1) = -30
    c: DistanceY(g0) = -19
    c: DistanceX(g0) = 31.08
FEATURE [PartDesign::Pocket] Pocket148
  BaseFeature = -> Clone068
  Direction = (0,0,-1)
  Length = 10
  Length2 = 5
  Midplane = true
  Profile = -> Sketch243
  ReferenceAxis = -> Sketch243 [N_Axis]
  Suppressed = false
  Type = 0
FEATURE [Sketcher::SketchObject] Sketch244
  ArcFitTolerance = 0
  AttachmentOffset = pos=(0,0,-5) rot=(0,0,1;0rad)
  AttachmentSupport = -> [XY_Plane253]
  FullyConstrained = true
  MakeInternals = false
  MapMode = 5
  Placement = pos=(0,0,-5) rot=(0,0,1;0rad)
  sketch-geometry (10):
    g0: ArcOfCircle CenterX=19 CenterY=19 CenterZ=0 NormalX=0 NormalY=0 NormalZ=1 AngleXU=0 Radius=9 StartAngle=3.14159 EndAngle=5.25009
    g1: LineSegment StartX=10 StartY=19 StartZ=0 EndX=10 EndY=30 EndZ=0
    g2: LineSegment StartX=10 StartY=30 StartZ=0 EndX=28 EndY=30 EndZ=0
    g3: LineSegment StartX=28 StartY=30 StartZ=0 EndX=28 EndY=19 EndZ=0
    g4: LineSegment StartX=23.6095 StartY=11.27 StartZ=0 EndX=40 EndY=11.27 EndZ=0
    g5: LineSegment StartX=40 StartY=11.27 StartZ=0 EndX=40 EndY=14.65 EndZ=0
    g6: LineSegment StartX=40 StartY=14.65 StartZ=0 EndX=26.8789 EndY=14.65 EndZ=0
    g7: ArcOfCircle CenterX=19 CenterY=19 CenterZ=0 NormalX=0 NormalY=0 NormalZ=1 AngleXU=0 Radius=9 StartAngle=5.77873 EndAngle=6.28319
    g8: GeomPoint [constr] X=19 Y=12.9 Z=0
    g9: Circle [constr] CenterX=19 CenterY=19 CenterZ=0 NormalX=0 NormalY=0 NormalZ=1 AngleXU=0 Radius=6.1
  constraints (27):
    c: Diameter(g0) = 18
    c: Vertical(g1)
    c: Coincident(g2,g1)
    c: Horizontal(g2)
    c: Coincident(g3,g2)
    c: Vertical(g3)
    c: DistanceY(g2) = 30
    c: Tangent(g0,g1) = 1.5708
    c: Horizontal(g4)
    c: Coincident(g5,g4)
    c: Vertical(g5)
    c: Coincident(g6,g5)
    c: Horizontal(g6)
    c: Equal(g0,g7)
    c: Coincident(g0,g4)
    c: Coincident(g7,g6)
    c: Coincident(g0,g7)
    c: Tangent(g7,g3) = 1.5708
    c: DistanceX(g5) = 40
    c: Vertical(g8,g0)
    c: DistanceY(g0,g8) = 1.63
    c: DistanceY(g8,g6) = 1.75
    c: Coincident(g9,g0)
    c: Diameter(g9) = 12.2
    c: PointOnObject(g8,g9)
    c: DistanceX(g0) = 19
    c: DistanceY(g0) = 19
FEATURE [PartDesign::Pocket] Pocket149
  BaseFeature = -> Pocket148
  Direction = (0,0,-1)
  Length = 10
  Length2 = 5
  Midplane = true
  Profile = -> Sketch244
  ReferenceAxis = -> Sketch244 [N_Axis]
  Suppressed = false
  Type = 0
FEATURE [PartDesign::Revolution] Revolution017
  Angle = 360
  Angle2 = 60
  Axis = (0,2e-16,1)
  Base = (31.08,-19,4e-15)
  BaseFeature = -> Pocket149
  Profile = -> Sketch242
  ReferenceAxis = -> Sketch242 [Edge1]
  Reversed = true
  Suppressed = false
  Type = 0
FEATURE [Sketcher::SketchObject] Sketch245
  ArcFitTolerance = 0
  AttachmentOffset = pos=(0,0,19) rot=(0,0,1;0rad)
  AttachmentSupport = -> [XZ_Plane253]
  FullyConstrained = true
  MakeInternals = false
  MapMode = 5
  Placement = pos=(0,-19,4.2e-15) rot=(1,0,0;1.5708rad)
  sketch-geometry (6):
    g0: LineSegment StartX=31.08 StartY=12.5 StartZ=0 EndX=31.08 EndY=-28 EndZ=0
    g1: LineSegment StartX=31.08 StartY=-28 StartZ=0 EndX=26.08 EndY=-28 EndZ=0
    g2: LineSegment StartX=26.08 StartY=-28 StartZ=0 EndX=26.08 EndY=-8 EndZ=0
    g3: LineSegment StartX=26.08 StartY=-8 StartZ=0 EndX=28.63 EndY=-8 EndZ=0
    g4: LineSegment StartX=28.63 StartY=-8 StartZ=0 EndX=28.63 EndY=12.5 EndZ=0
    g5: LineSegment StartX=28.63 StartY=12.5 StartZ=0 EndX=31.08 EndY=12.5 EndZ=0
  constraints (18):
    c: Vertical(g0)
    c: Coincident(g0,g1)
    c: Horizontal(g1)
    c: Coincident(g1,g2)
    c: Vertical(g2)
    c: Coincident(g2,g3)
    c: Horizontal(g3)
    c: Coincident(g3,g4)
    c: Coincident(g4,g5)
    c: Coincident(g5,g0)
    c: Horizontal(g5)
    c: DistanceY(g4,g4) = 20.5
    c: DistanceX(g5,g5) = 2.45
    c: DistanceX(g0) = 31.08
    c: DistanceY(g0) = -28
    c: DistanceX(g1,g1) = 5
    c: DistanceY(g4) = 12.5
    c: Vertical(g4)
FEATURE [Sketcher::SketchObject] Sketch246
  ArcFitTolerance = 0
  AttachmentOffset = pos=(0,0,-19) rot=(0,0,1;0rad)
  AttachmentSupport = -> [XZ_Plane253]
  FullyConstrained = true
  MakeInternals = false
  MapMode = 5
  Placement = pos=(0,19,-4.2e-15) rot=(1,0,0;1.5708rad)
  sketch-geometry (6):
    g0: LineSegment StartX=19 StartY=3 StartZ=0 EndX=19 EndY=-28 EndZ=0
    g1: LineSegment StartX=19 StartY=-28 StartZ=0 EndX=14 EndY=-28 EndZ=0
    g2: LineSegment StartX=14 StartY=-28 StartZ=0 EndX=14 EndY=-17.5 EndZ=0
    g3: LineSegment StartX=14 StartY=-17.5 StartZ=0 EndX=16.55 EndY=-17.5 EndZ=0
    g4: LineSegment StartX=16.55 StartY=-17.5 StartZ=0 EndX=16.55 EndY=3 EndZ=0
    g5: LineSegment StartX=16.55 StartY=3 StartZ=0 EndX=19 EndY=3 EndZ=0
  constraints (18):
    c: Vertical(g0)
    c: Coincident(g0,g1)
    c: Horizontal(g1)
    c: Coincident(g1,g2)
    c: Vertical(g2)
    c: Coincident(g2,g3)
    c: Horizontal(g3)
    c: Coincident(g3,g4)
    c: Vertical(g4)
    c: Coincident(g4,g5)
    c: Coincident(g5,g0)
    c: Horizontal(g5)
    c: DistanceX(g5,g5) = 2.45
    c: DistanceX(g0) = 19
    c: DistanceX(g1,g1) = 5
    c: DistanceY(g0) = 3
    c: DistanceY(g4,g4) = 20.5
    c: DistanceY(g0) = -28
FEATURE [Sketcher::SketchObject] Sketch247
  ArcFitTolerance = 0
  AttachmentOffset = pos=(0,0,-19) rot=(0,0,1;0rad)
  AttachmentSupport = -> [XZ_Plane253]
  FullyConstrained = true
  MakeInternals = false
  MapMode = 5
  Placement = pos=(0,19,-4.2e-15) rot=(1,0,0;1.5708rad)
  sketch-geometry (9):
    g0: GeomPoint [constr] X=19 Y=-5 Z=0
    g1: LineSegment StartX=19 StartY=-2e-16 StartZ=0 EndX=19 EndY=-0.75 EndZ=0
    g2: LineSegment StartX=19 StartY=-0.75 StartZ=0 EndX=23 EndY=-0.75 EndZ=0
    g3: LineSegment StartX=23 StartY=-0.75 StartZ=0 EndX=23.75 EndY=-2e-16 EndZ=0
    g4: LineSegment StartX=23.75 StartY=-2e-16 StartZ=0 EndX=19 EndY=-2e-16 EndZ=0
    g5: LineSegment StartX=19 StartY=-10 StartZ=0 EndX=19 EndY=-9.25 EndZ=0
    g6: LineSegment StartX=19 StartY=-9.25 StartZ=0 EndX=23 EndY=-9.25 EndZ=0
    g7: LineSegment StartX=23 StartY=-9.25 StartZ=0 EndX=23.75 EndY=-10 EndZ=0
    g8: LineSegment StartX=23.75 StartY=-10 StartZ=0 EndX=19 EndY=-10 EndZ=0
  constraints (25):
    c: DistanceX(g0) = 19
    c: DistanceY(g0) = -5
    c: Vertical(g1)
    c: Coincident(g1,g2)
    c: Horizontal(g2)
    c: Coincident(g2,g3)
    c: Coincident(g3,g4)
    c: Coincident(g4,g1)
    c: Horizontal(g4)
    c: Vertical(g5)
    c: Coincident(g5,g6)
    c: Horizontal(g6)
    c: Coincident(g6,g7)
    c: Coincident(g7,g8)
    c: Coincident(g8,g5)
    c: Horizontal(g8)
    c: Symmetric(g5,g1,g0)
    c: Vertical(g5,g1)
    c: Angle(g7) = -0.785398
    c: DistanceX(g6,g6) = 4
    c: Equal(g1,g5)
    c: Perpendicular(g7,g3)
    c: Equal(g2,g6)
    c: DistanceY(g5,g1) = 10
    c: DistanceY(g5,g1) = 8.5
FEATURE [PartDesign::Revolution] Revolution018
  Angle = 360
  Angle2 = 60
  Axis = (0,-2e-16,-1)
  Base = (19,19,-4.4e-15)
  BaseFeature = -> Revolution017
  Profile = -> Sketch247
  ReferenceAxis = -> Sketch247 [Edge1]
  Reversed = true
  Suppressed = false
  Type = 0
FEATURE [PartDesign::Groove] Groove007
  Angle = 360
  Angle2 = 60
  Axis = (0,-2e-16,-1)
  Base = (31.08,-19,12.5)
  BaseFeature = -> Revolution018
  Profile = -> Sketch245
  ReferenceAxis = -> Sketch245 [Edge1]
  Suppressed = false
  Type = 0
FEATURE [PartDesign::Groove] Groove008
  Angle = 360
  Angle2 = 60
  Axis = (0,-2e-16,-1)
  Base = (19,19,3)
  BaseFeature = -> Groove007
  Profile = -> Sketch246
  ReferenceAxis = -> Sketch246 [Edge1]
  Suppressed = false
  Type = 0
FEATURE [Sketcher::SketchObject] Sketch289
  ArcFitTolerance = 0
  AttachmentSupport = -> [XZ_Plane253]
  FullyConstrained = true
  MakeInternals = false
  MapMode = 5
  Placement = pos=(0,0,0) rot=(1,0,0;1.5708rad)
  sketch-geometry (9):
    g0: LineSegment StartX=12 StartY=9 StartZ=0 EndX=13 EndY=9 EndZ=0
    g1: LineSegment StartX=14 StartY=8 StartZ=0 EndX=14 EndY=2 EndZ=0
    g2: LineSegment StartX=13 StartY=1 StartZ=0 EndX=12 EndY=1 EndZ=0
    g3: LineSegment StartX=12 StartY=1 StartZ=0 EndX=12 EndY=9 EndZ=0
    g4: ArcOfCircle CenterX=13 CenterY=8 CenterZ=0 NormalX=0 NormalY=0 NormalZ=1 AngleXU=0 Radius=1 StartAngle=0 EndAngle=1.5708
    g5: GeomPoint [constr] X=14 Y=9 Z=0
    g6: ArcOfCircle CenterX=13 CenterY=2 CenterZ=0 NormalX=0 NormalY=0 NormalZ=1 AngleXU=0 Radius=1 StartAngle=4.71239 EndAngle=6.28319
    g7: GeomPoint [constr] X=14 Y=1 Z=0
    g8: GeomPoint [constr] X=12 Y=5 Z=0
  constraints (21):
    c: Coincident(g2,g3)
    c: Coincident(g3,g0)
    c: Horizontal(g0)
    c: Horizontal(g2)
    c: Vertical(g1)
    c: Vertical(g3)
    c: PointOnObject(g5,g0)
    c: PointOnObject(g5,g1)
    c: Tangent(g0,g4) = 1.5708
    c: Tangent(g1,g4) = 1.5708
    c: PointOnObject(g7,g1)
    c: PointOnObject(g7,g2)
    c: Tangent(g1,g6) = 1.5708
    c: Tangent(g2,g6) = 1.5708
    c: Equal(g4,g6)
    c: Radius(g6) = 1
    c: DistanceY(g3,g3) = 8
    c: DistanceX(g2,g2) = 1
    c: Symmetric(g2,g0,g8)
    c: DistanceY(g8) = 5
    c: DistanceX(g8) = 12
FEATURE [PartDesign::Pocket] Pocket179
  BaseFeature = -> Groove008
  Direction = (0,1,-2e-16)
  Length = 5
  Length2 = 5
  Midplane = true
  Profile = -> Sketch289
  ReferenceAxis = -> Sketch289 [N_Axis]
  Suppressed = false
  Type = 1
FEATURE [PartDesign::Body] Body120  label="y-carriage-left"
  AllowCompound = false
  Group = -> [Clone068,Sketch242,Sketch243,Sketch244,Sketch245,Sketch246,Sketch247,Pocket148,Pocket149,Revolution017,Revolution018,Groove007,Groove008,Sketch289,Pocket179]
  Origin = -> Origin254
  Tip = -> Pocket179
COMPONENT P4 — recipe-attached ("main-vslot-right", modeled in this document).
Construction recipe (the document's own serialized feature program — sketch geometry with constraints, then the solid features built on it; lengths are millimeters unless a unit is written):

FEATURE [PartDesign::FeatureBase] Clone069
  BaseFeature = -> Body118
  Suppressed = false
FEATURE [Sketcher::SketchObject] Sketch248
  ArcFitTolerance = 0
  AttachmentOffset = pos=(0,0,19) rot=(0,0,1;0rad)
  AttachmentSupport = -> [XZ_Plane254]
  FullyConstrained = true
  MakeInternals = false
  MapMode = 5
  Placement = pos=(0,-19,4.2e-15) rot=(1,0,0;1.5708rad)
  sketch-geometry (10):
    g0: GeomPoint [constr] X=31.08 Y=-10 Z=0
    g1: GeomPoint [constr] X=31.08 Y=-5 Z=0
    g2: LineSegment StartX=31.08 StartY=-10 StartZ=0 EndX=31.08 EndY=-9.25 EndZ=0
    g3: LineSegment StartX=31.08 StartY=-9.25 StartZ=0 EndX=35.08 EndY=-9.25 EndZ=0
    g4: LineSegment StartX=35.08 StartY=-9.25 StartZ=0 EndX=35.83 EndY=-10 EndZ=0
    g5: LineSegment StartX=35.83 StartY=-10 StartZ=0 EndX=31.08 EndY=-10 EndZ=0
    g6: LineSegment StartX=31.08 StartY=-0.75 StartZ=0 EndX=31.08 EndY=2e-16 EndZ=0
    g7: LineSegment StartX=31.08 StartY=2e-16 StartZ=0 EndX=35.83 EndY=2e-16 EndZ=0
    g8: LineSegment StartX=35.83 StartY=2e-16 StartZ=0 EndX=35.08 EndY=-0.75 EndZ=0
    g9: LineSegment StartX=35.08 StartY=-0.75 StartZ=0 EndX=31.08 EndY=-0.75 EndZ=0
  constraints (26):
    c: Vertical(g1,g0)
    c: Coincident(g2,g0)
    c: Vertical(g2)
    c: Coincident(g2,g3)
    c: Horizontal(g3)
    c: Coincident(g3,g4)
    c: Coincident(g4,g5)
    c: Coincident(g5,g2)
    c: Horizontal(g5)
    c: Coincident(g6,g7)
    c: Horizontal(g7)
    c: Coincident(g7,g8)
    c: Coincident(g8,g9)
    c: Coincident(g9,g6)
    c: Vertical(g6)
    c: Horizontal(g9)
    c: Equal(g2,g6)
    c: DistanceY(g-1,g1) = -5
    c: DistanceX(g1) = 31.08
    c: DistanceX(g3,g3) = 4
    c: Angle(g4) = -0.785398
    c: Perpendicular(g4,g8)
    c: Symmetric(g6,g2,g1)
    c: DistanceY(g2,g6) = 8.5
    c: DistanceY(g2,g6) = 10
    c: Vertical(g8,g3)
FEATURE [Sketcher::SketchObject] Sketch249
  ArcFitTolerance = 0
  AttachmentOffset = pos=(0,0,-5) rot=(0,0,1;0rad)
  AttachmentSupport = -> [XY_Plane254]
  FullyConstrained = true
  MakeInternals = false
  MapMode = 5
  Placement = pos=(0,0,-5) rot=(0,0,1;0rad)
  sketch-geometry (5):
    g0: ArcOfCircle CenterX=31.08 CenterY=-19 CenterZ=0 NormalX=0 NormalY=0 NormalZ=1 AngleXU=0 Radius=9 StartAngle=1.5708 EndAngle=3.14159
    g1: LineSegment StartX=22.08 StartY=-19 StartZ=0 EndX=22.08 EndY=-30 EndZ=0
    g2: LineSegment StartX=22.08 StartY=-30 StartZ=0 EndX=40.08 EndY=-30 EndZ=0
    g3: LineSegment StartX=40.08 StartY=-30 StartZ=0 EndX=40.08 EndY=-10 EndZ=0
    g4: LineSegment StartX=40.08 StartY=-10 StartZ=0 EndX=31.08 EndY=-10 EndZ=0
  constraints (14):
    c: Diameter(g0) = 18
    c: Vertical(g1)
    c: Coincident(g2,g1)
    c: Horizontal(g2)
    c: Coincident(g3,g2)
    c: Vertical(g3)
    c: Coincident(g4,g3)
    c: Horizontal(g4)
    c: Tangent(g0,g1) = -1.5708
    c: Tangent(g0,g4) = -1.5708
    c: Tangent(g3,g0)
    c: DistanceY(g1) = -30
    c: DistanceY(g0) = -19
    c: DistanceX(g0) = 31.08
FEATURE [PartDesign::Pocket] Pocket150
  BaseFeature = -> Clone069
  Direction = (0,0,-1)
  Length = 10
  Length2 = 5
  Midplane = true
  Profile = -> Sketch249
  ReferenceAxis = -> Sketch249 [N_Axis]
  Suppressed = false
  Type = 0
FEATURE [Sketcher::SketchObject] Sketch250
  ArcFitTolerance = 0
  AttachmentOffset = pos=(0,0,5) rot=(0,0,1;0rad)
  AttachmentSupport = -> [XY_Plane254]
  FullyConstrained = true
  MakeInternals = false
  MapMode = 5
  Placement = pos=(0,0,5) rot=(0,0,1;0rad)
  sketch-geometry (10):
    g0: ArcOfCircle CenterX=19 CenterY=19 CenterZ=0 NormalX=0 NormalY=0 NormalZ=1 AngleXU=0 Radius=9 StartAngle=3.14159 EndAngle=5.25009
    g1: LineSegment StartX=10 StartY=19 StartZ=0 EndX=10 EndY=30 EndZ=0
    g2: LineSegment StartX=10 StartY=30 StartZ=0 EndX=28 EndY=30 EndZ=0
    g3: LineSegment StartX=28 StartY=30 StartZ=0 EndX=28 EndY=19 EndZ=0
    g4: LineSegment StartX=23.6095 StartY=11.27 StartZ=0 EndX=40 EndY=11.27 EndZ=0
    g5: LineSegment StartX=40 StartY=11.27 StartZ=0 EndX=40 EndY=14.65 EndZ=0
    g6: LineSegment StartX=40 StartY=14.65 StartZ=0 EndX=26.8789 EndY=14.65 EndZ=0
    g7: ArcOfCircle CenterX=19 CenterY=19 CenterZ=0 NormalX=0 NormalY=0 NormalZ=1 AngleXU=0 Radius=9 StartAngle=5.77873 EndAngle=6.28319
    g8: GeomPoint [constr] X=19 Y=12.9 Z=0
    g9: Circle [constr] CenterX=19 CenterY=19 CenterZ=0 NormalX=0 NormalY=0 NormalZ=1 AngleXU=0 Radius=6.1
  constraints (27):
    c: Diameter(g0) = 18
    c: Vertical(g1)
    c: Coincident(g2,g1)
    c: Horizontal(g2)
    c: Coincident(g3,g2)
    c: Vertical(g3)
    c: DistanceY(g2) = 30
    c: Tangent(g0,g1) = 1.5708
    c: Horizontal(g4)
    c: Coincident(g5,g4)
    c: Vertical(g5)
    c: Coincident(g6,g5)
    c: Horizontal(g6)
    c: Equal(g0,g7)
    c: Coincident(g0,g4)
    c: Coincident(g7,g6)
    c: Coincident(g0,g7)
    c: Tangent(g7,g3) = 1.5708
    c: DistanceX(g5) = 40
    c: Vertical(g8,g0)
    c: DistanceY(g0,g8) = 1.63
    c: DistanceY(g8,g6) = 1.75
    c: Coincident(g9,g0)
    c: Diameter(g9) = 12.2
    c: PointOnObject(g8,g9)
    c: DistanceX(g0) = 19
    c: DistanceY(g0) = 19
FEATURE [PartDesign::Pocket] Pocket151
  BaseFeature = -> Pocket150
  Direction = (0,0,-1)
  Length = 10
  Length2 = 5
  Midplane = true
  Profile = -> Sketch250
  ReferenceAxis = -> Sketch250 [N_Axis]
  Suppressed = false
  Type = 0
FEATURE [PartDesign::Revolution] Revolution019
  Angle = 360
  Angle2 = 60
  Axis = (0,2e-16,1)
  Base = (31.08,-19,-0.75)
  BaseFeature = -> Pocket151
  Profile = -> Sketch248
  ReferenceAxis = -> Sketch248 [Edge5]
  Reversed = true
  Suppressed = false
  Type = 0
FEATURE [Sketcher::SketchObject] Sketch251
  ArcFitTolerance = 0
  AttachmentOffset = pos=(0,0,-19) rot=(0,0,1;0rad)
  AttachmentSupport = -> [XZ_Plane254]
  FullyConstrained = true
  MakeInternals = false
  MapMode = 5
  Placement = pos=(0,19,-4.2e-15) rot=(1,0,0;1.5708rad)
  sketch-geometry (6):
    g0: LineSegment StartX=19 StartY=12.5 StartZ=0 EndX=19 EndY=-28 EndZ=0
    g1: LineSegment StartX=19 StartY=-28 StartZ=0 EndX=14 EndY=-28 EndZ=0
    g2: LineSegment StartX=14 StartY=-28 StartZ=0 EndX=14 EndY=-8 EndZ=0
    g3: LineSegment StartX=14 StartY=-8 StartZ=0 EndX=16.55 EndY=-8 EndZ=0
    g4: LineSegment StartX=16.55 StartY=-8 StartZ=0 EndX=16.55 EndY=12.5 EndZ=0
    g5: LineSegment StartX=16.55 StartY=12.5 StartZ=0 EndX=19 EndY=12.5 EndZ=0
  constraints (18):
    c: Vertical(g0)
    c: Coincident(g0,g1)
    c: Horizontal(g1)
    c: Coincident(g1,g2)
    c: Vertical(g2)
    c: Coincident(g2,g3)
    c: Horizontal(g3)
    c: Coincident(g3,g4)
    c: Coincident(g4,g5)
    c: Coincident(g5,g0)
    c: Horizontal(g5)
    c: DistanceY(g4,g4) = 20.5
    c: DistanceX(g5,g5) = 2.45
    c: DistanceX(g0) = 19
    c: DistanceY(g0) = -28
    c: DistanceX(g1,g1) = 5
    c: DistanceY(g4) = 12.5
    c: Vertical(g4)
FEATURE [Sketcher::SketchObject] Sketch252
  ArcFitTolerance = 0
  AttachmentOffset = pos=(0,0,19) rot=(0,0,1;0rad)
  AttachmentSupport = -> [XZ_Plane254]
  FullyConstrained = true
  MakeInternals = false
  MapMode = 5
  Placement = pos=(0,-19,4.2e-15) rot=(1,0,0;1.5708rad)
  sketch-geometry (6):
    g0: LineSegment StartX=31.08 StartY=3 StartZ=0 EndX=31.08 EndY=-28 EndZ=0
    g1: LineSegment StartX=31.08 StartY=-28 StartZ=0 EndX=26.08 EndY=-28 EndZ=0
    g2: LineSegment StartX=26.08 StartY=-28 StartZ=0 EndX=26.08 EndY=-17.5 EndZ=0
    g3: LineSegment StartX=26.08 StartY=-17.5 StartZ=0 EndX=28.63 EndY=-17.5 EndZ=0
    g4: LineSegment StartX=28.63 StartY=-17.5 StartZ=0 EndX=28.63 EndY=3 EndZ=0
    g5: LineSegment StartX=28.63 StartY=3 StartZ=0 EndX=31.08 EndY=3 EndZ=0
  constraints (18):
    c: Vertical(g0)
    c: Coincident(g0,g1)
    c: Horizontal(g1)
    c: Coincident(g1,g2)
    c: Vertical(g2)
    c: Coincident(g2,g3)
    c: Horizontal(g3)
    c: Coincident(g3,g4)
    c: Vertical(g4)
    c: Coincident(g4,g5)
    c: Coincident(g5,g0)
    c: Horizontal(g5)
    c: DistanceX(g5,g5) = 2.45
    c: DistanceX(g0) = 31.08
    c: DistanceX(g1,g1) = 5
    c: DistanceY(g0) = 3
    c: DistanceY(g4,g4) = 20.5
    c: DistanceY(g0) = -28
FEATURE [Sketcher::SketchObject] Sketch253
  ArcFitTolerance = 0
  AttachmentOffset = pos=(0,0,-19) rot=(0,0,1;0rad)
  AttachmentSupport = -> [XZ_Plane254]
  FullyConstrained = true
  MakeInternals = false
  MapMode = 5
  Placement = pos=(0,19,-4.2e-15) rot=(1,0,0;1.5708rad)
  sketch-geometry (9):
    g0: GeomPoint [constr] X=19 Y=5 Z=0
    g1: LineSegment StartX=19 StartY=10 StartZ=0 EndX=19 EndY=9.25 EndZ=0
    g2: LineSegment StartX=19 StartY=9.25 StartZ=0 EndX=23 EndY=9.25 EndZ=0
    g3: LineSegment StartX=23 StartY=9.25 StartZ=0 EndX=23.75 EndY=10 EndZ=0
    g4: LineSegment StartX=23.75 StartY=10 StartZ=0 EndX=19 EndY=10 EndZ=0
    g5: LineSegment StartX=19 StartY=1e-16 StartZ=0 EndX=19 EndY=0.75 EndZ=0
    g6: LineSegment StartX=19 StartY=0.75 StartZ=0 EndX=23 EndY=0.75 EndZ=0
    g7: LineSegment StartX=23 StartY=0.75 StartZ=0 EndX=23.75 EndY=1e-16 EndZ=0
    g8: LineSegment StartX=23.75 StartY=1e-16 StartZ=0 EndX=19 EndY=1e-16 EndZ=0
  constraints (25):
    c: DistanceX(g0) = 19
    c: DistanceY(g0) = 5
    c: Vertical(g1)
    c: Coincident(g1,g2)
    c: Horizontal(g2)
    c: Coincident(g2,g3)
    c: Coincident(g3,g4)
    c: Coincident(g4,g1)
    c: Horizontal(g4)
    c: Vertical(g5)
    c: Coincident(g5,g6)
    c: Horizontal(g6)
    c: Coincident(g6,g7)
    c: Coincident(g7,g8)
    c: Coincident(g8,g5)
    c: Horizontal(g8)
    c: Symmetric(g5,g1,g0)
    c: Vertical(g5,g1)
    c: Angle(g7) = -0.785398
    c: DistanceX(g6,g6) = 4
    c: Equal(g1,g5)
    c: Perpendicular(g7,g3)
    c: Equal(g2,g6)
    c: DistanceY(g5,g1) = 10
    c: DistanceY(g5,g1) = 8.5
FEATURE [PartDesign::Revolution] Revolution020
  Angle = 360
  Angle2 = 60
  Axis = (0,-2e-16,-1)
  Base = (19,19,10)
  BaseFeature = -> Revolution019
  Profile = -> Sketch253
  ReferenceAxis = -> Sketch253 [Edge1]
  Reversed = true
  Suppressed = false
  Type = 0
FEATURE [PartDesign::Groove] Groove009
  Angle = 360
  Angle2 = 60
  Axis = (0,-2e-16,-1)
  Base = (19,19,12.5)
  BaseFeature = -> Revolution020
  Profile = -> Sketch251
  ReferenceAxis = -> Sketch251 [Edge1]
  Suppressed = false
  Type = 0
FEATURE [PartDesign::Groove] Groove010
  Angle = 360
  Angle2 = 60
  Axis = (0,-2e-16,-1)
  Base = (31.08,-19,3)
  BaseFeature = -> Groove009
  Profile = -> Sketch252
  ReferenceAxis = -> Sketch252 [Edge1]
  Suppressed = false
  Type = 0
FEATURE [Sketcher::SketchObject] Sketch290
  ArcFitTolerance = 0
  AttachmentSupport = -> [XZ_Plane254]
  FullyConstrained = true
  MakeInternals = false
  MapMode = 5
  Placement = pos=(0,0,0) rot=(1,0,0;1.5708rad)
  sketch-geometry (9):
    g0: LineSegment StartX=12 StartY=-1 StartZ=0 EndX=13 EndY=-1 EndZ=0
    g1: LineSegment StartX=14 StartY=-2 StartZ=0 EndX=14 EndY=-8 EndZ=0
    g2: LineSegment StartX=13 StartY=-9 StartZ=0 EndX=12 EndY=-9 EndZ=0
    g3: LineSegment StartX=12 StartY=-9 StartZ=0 EndX=12 EndY=-1 EndZ=0
    g4: ArcOfCircle CenterX=13 CenterY=-2 CenterZ=0 NormalX=0 NormalY=0 NormalZ=1 AngleXU=0 Radius=1 StartAngle=0 EndAngle=1.5708
    g5: GeomPoint [constr] X=14 Y=-1 Z=0
    g6: ArcOfCircle CenterX=13 CenterY=-8 CenterZ=0 NormalX=0 NormalY=0 NormalZ=1 AngleXU=0 Radius=1 StartAngle=4.71239 EndAngle=6.28319
    g7: GeomPoint [constr] X=14 Y=-9 Z=0
    g8: GeomPoint [constr] X=12 Y=-5 Z=0
  constraints (21):
    c: Coincident(g2,g3)
    c: Coincident(g3,g0)
    c: Horizontal(g0)
    c: Horizontal(g2)
    c: Vertical(g1)
    c: Vertical(g3)
    c: DistanceX(g0,g5) = 2
    c: DistanceY(g3,g3) = 8
    c: PointOnObject(g5,g0)
    c: PointOnObject(g5,g1)
    c: Tangent(g0,g4) = 1.5708
    c: Tangent(g1,g4) = 1.5708
    c: PointOnObject(g7,g1)
    c: PointOnObject(g7,g2)
    c: Tangent(g1,g6) = 1.5708
    c: Tangent(g2,g6) = 1.5708
    c: Equal(g6,g4)
    c: Radius(g4) = 1
    c: Symmetric(g2,g0,g8)
    c: DistanceX(g8) = 12
    c: DistanceY(g8) = -5
FEATURE [PartDesign::Pocket] Pocket180
  BaseFeature = -> Groove010
  Direction = (0,1,-2e-16)
  Length = 5
  Length2 = 5
  Midplane = true
  Profile = -> Sketch290
  ReferenceAxis = -> Sketch290 [N_Axis]
  Suppressed = false
  Type = 1
FEATURE [PartDesign::Body] Body121
  AllowCompound = false
  Group = -> [Clone069,Sketch248,Sketch249,Sketch250,Sketch251,Sketch252,Sketch253,Pocket150,Pocket151,Revolution019,Revolution020,Groove009,Groove010,Sketch290,Pocket180]
  Origin = -> Origin255
  Tip = -> Pocket180
COMPONENT P5 — recipe-attached ("main-rail-left", modeled in this document).
Construction recipe (the document's own serialized feature program — sketch geometry with constraints, then the solid features built on it; lengths are millimeters unless a unit is written):

FEATURE [Sketcher::SketchObject] Sketch474
  ArcFitTolerance = 0
  AttachmentOffset = pos=(0,0,5) rot=(0,0,1;0rad)
  AttachmentSupport = -> [XY_Plane294]
  FullyConstrained = true
  MakeInternals = false
  MapMode = 5
  Placement = pos=(0,0,5) rot=(0,0,1;0rad)
  sketch-geometry (5):
    g0: ArcOfCircle CenterX=31.83 CenterY=-19 CenterZ=0 NormalX=0 NormalY=0 NormalZ=1 AngleXU=0 Radius=9 StartAngle=1.5708 EndAngle=3.14159
    g1: LineSegment StartX=22.83 StartY=-19 StartZ=0 EndX=22.83 EndY=-30 EndZ=0
    g2: LineSegment StartX=22.83 StartY=-30 StartZ=0 EndX=40.83 EndY=-30 EndZ=0
    g3: LineSegment StartX=40.83 StartY=-30 StartZ=0 EndX=40.83 EndY=-10 EndZ=0
    g4: LineSegment StartX=40.83 StartY=-10 StartZ=0 EndX=31.83 EndY=-10 EndZ=0
  constraints (14):
    c: Diameter(g0) = 18
    c: Vertical(g1)
    c: Coincident(g2,g1)
    c: Horizontal(g2)
    c: Coincident(g3,g2)
    c: Vertical(g3)
    c: Coincident(g4,g3)
    c: Horizontal(g4)
    c: Tangent(g0,g1) = -1.5708
    c: Tangent(g0,g4) = -1.5708
    c: Tangent(g3,g0)
    c: DistanceY(g1) = -30
    c: DistanceY(g0) = -19
    c: DistanceX(g0) = 31.83
FEATURE [Sketcher::SketchObject] Sketch475
  ArcFitTolerance = 0
  AttachmentOffset = pos=(0,0,-5) rot=(0,0,1;0rad)
  AttachmentSupport = -> [XY_Plane294]
  FullyConstrained = true
  MakeInternals = false
  MapMode = 5
  Placement = pos=(0,0,-5) rot=(0,0,1;0rad)
  sketch-geometry (10):
    g0: ArcOfCircle CenterX=19 CenterY=19 CenterZ=0 NormalX=0 NormalY=0 NormalZ=1 AngleXU=0 Radius=9 StartAngle=3.14159 EndAngle=5.25009
    g1: LineSegment StartX=10 StartY=19 StartZ=0 EndX=10 EndY=30 EndZ=0
    g2: LineSegment StartX=10 StartY=30 StartZ=0 EndX=28 EndY=30 EndZ=0
    g3: LineSegment StartX=28 StartY=30 StartZ=0 EndX=28 EndY=19 EndZ=0
    g4: LineSegment StartX=23.6095 StartY=11.27 StartZ=0 EndX=40 EndY=11.27 EndZ=0
    g5: LineSegment StartX=40 StartY=11.27 StartZ=0 EndX=40 EndY=14.65 EndZ=0
    g6: LineSegment StartX=40 StartY=14.65 StartZ=0 EndX=26.8789 EndY=14.65 EndZ=0
    g7: ArcOfCircle CenterX=19 CenterY=19 CenterZ=0 NormalX=0 NormalY=0 NormalZ=1 AngleXU=0 Radius=9 StartAngle=5.77873 EndAngle=6.28319
    g8: GeomPoint [constr] X=19 Y=12.9 Z=0
    g9: Circle [constr] CenterX=19 CenterY=19 CenterZ=0 NormalX=0 NormalY=0 NormalZ=1 AngleXU=0 Radius=6.1
  constraints (27):
    c: Diameter(g0) = 18
    c: Vertical(g1)
    c: Coincident(g2,g1)
    c: Horizontal(g2)
    c: Coincident(g3,g2)
    c: Vertical(g3)
    c: DistanceY(g2) = 30
    c: Tangent(g0,g1) = 1.5708
    c: Horizontal(g4)
    c: Coincident(g5,g4)
    c: Vertical(g5)
    c: Coincident(g6,g5)
    c: Horizontal(g6)
    c: Equal(g0,g7)
    c: Coincident(g0,g4)
    c: Coincident(g7,g6)
    c: Coincident(g0,g7)
    c: Tangent(g7,g3) = 1.5708
    c: DistanceX(g5) = 40
    c: Vertical(g8,g0)
    c: DistanceY(g0,g8) = 1.63
    c: DistanceY(g8,g6) = 1.75
    c: Coincident(g9,g0)
    c: Diameter(g9) = 12.2
    c: PointOnObject(g8,g9)
    c: DistanceX(g0) = 19
    c: DistanceY(g0) = 19
FEATURE [Sketcher::SketchObject] Sketch476
  ArcFitTolerance = 0
  AttachmentOffset = pos=(0,0,19) rot=(0,0,1;0rad)
  AttachmentSupport = -> [XZ_Plane294]
  FullyConstrained = true
  MakeInternals = false
  MapMode = 5
  Placement = pos=(0,-19,4.2e-15) rot=(1,0,0;1.5708rad)
  sketch-geometry (10):
    g0: GeomPoint [constr] X=31.83 Y=1e-16 Z=0
    g1: GeomPoint [constr] X=31.83 Y=5 Z=0
    g2: LineSegment StartX=31.83 StartY=1e-16 StartZ=0 EndX=31.83 EndY=0.75 EndZ=0
    g3: LineSegment StartX=31.83 StartY=0.75 StartZ=0 EndX=35.83 EndY=0.75 EndZ=0
    g4: LineSegment StartX=35.83 StartY=0.75 StartZ=0 EndX=36.58 EndY=1e-16 EndZ=0
    g5: LineSegment StartX=36.58 StartY=1e-16 StartZ=0 EndX=31.83 EndY=1e-16 EndZ=0
    g6: LineSegment StartX=31.83 StartY=10 StartZ=0 EndX=31.83 EndY=9.25 EndZ=0
    g7: LineSegment StartX=31.83 StartY=9.25 StartZ=0 EndX=35.83 EndY=9.25 EndZ=0
    g8: LineSegment StartX=35.83 StartY=9.25 StartZ=0 EndX=36.58 EndY=10 EndZ=0
    g9: LineSegment StartX=36.58 StartY=10 StartZ=0 EndX=31.83 EndY=10 EndZ=0
  constraints (26):
    c: Vertical(g1,g0)
    c: Coincident(g2,g0)
    c: Vertical(g2)
    c: Coincident(g2,g3)
    c: Horizontal(g3)
    c: Coincident(g3,g4)
    c: Coincident(g4,g5)
    c: Coincident(g5,g2)
    c: Horizontal(g5)
    c: Coincident(g6,g7)
    c: Horizontal(g7)
    c: Coincident(g7,g8)
    c: Coincident(g8,g9)
    c: Coincident(g9,g6)
    c: Vertical(g6)
    c: Horizontal(g9)
    c: Symmetric(g2,g6,g1)
    c: Equal(g2,g6)
    c: DistanceY(g-1,g1) = 5
    c: DistanceX(g1) = 31.83
    c: DistanceY(g2,g6) = 10
    c: DistanceX(g3,g3) = 4
    c: Angle(g4) = -0.785398
    c: Perpendicular(g4,g8)
    c: Equal(g9,g5)
    c: DistanceY(g2,g6) = 8.5
FEATURE [Sketcher::SketchObject] Sketch477
  ArcFitTolerance = 0
  AttachmentOffset = pos=(0,0,-19) rot=(0,0,1;0rad)
  AttachmentSupport = -> [XZ_Plane294]
  FullyConstrained = true
  MakeInternals = false
  MapMode = 5
  Placement = pos=(0,19,-4.2e-15) rot=(1,0,0;1.5708rad)
  sketch-geometry (9):
    g0: GeomPoint [constr] X=19 Y=-5 Z=0
    g1: LineSegment StartX=19 StartY=-2e-16 StartZ=0 EndX=19 EndY=-0.75 EndZ=0
    g2: LineSegment StartX=19 StartY=-0.75 StartZ=0 EndX=23 EndY=-0.75 EndZ=0
    g3: LineSegment StartX=23 StartY=-0.75 StartZ=0 EndX=23.75 EndY=-2e-16 EndZ=0
    g4: LineSegment StartX=23.75 StartY=-2e-16 StartZ=0 EndX=19 EndY=-2e-16 EndZ=0
    g5: LineSegment StartX=19 StartY=-10 StartZ=0 EndX=19 EndY=-9.25 EndZ=0
    g6: LineSegment StartX=19 StartY=-9.25 StartZ=0 EndX=23 EndY=-9.25 EndZ=0
    g7: LineSegment StartX=23 StartY=-9.25 StartZ=0 EndX=23.75 EndY=-10 EndZ=0
    g8: LineSegment StartX=23.75 StartY=-10 StartZ=0 EndX=19 EndY=-10 EndZ=0
  constraints (25):
    c: DistanceX(g0) = 19
    c: DistanceY(g0) = -5
    c: Vertical(g1)
    c: Coincident(g1,g2)
    c: Horizontal(g2)
    c: Coincident(g2,g3)
    c: Coincident(g3,g4)
    c: Coincident(g4,g1)
    c: Horizontal(g4)
    c: Vertical(g5)
    c: Coincident(g5,g6)
    c: Horizontal(g6)
    c: Coincident(g6,g7)
    c: Coincident(g7,g8)
    c: Coincident(g8,g5)
    c: Horizontal(g8)
    c: Symmetric(g5,g1,g0)
    c: Vertical(g5,g1)
    c: Angle(g7) = -0.785398
    c: DistanceX(g6,g6) = 4
    c: Equal(g1,g5)
    c: Perpendicular(g7,g3)
    c: Equal(g2,g6)
    c: DistanceY(g5,g1) = 10
    c: DistanceY(g5,g1) = 8.5
FEATURE [Sketcher::SketchObject] Sketch478
  ArcFitTolerance = 0
  AttachmentOffset = pos=(0,0,19) rot=(0,0,1;0rad)
  AttachmentSupport = -> [XZ_Plane294]
  FullyConstrained = true
  MakeInternals = false
  MapMode = 5
  Placement = pos=(0,-19,4.2e-15) rot=(1,0,0;1.5708rad)
  sketch-geometry (6):
    g0: LineSegment StartX=31.83 StartY=12.5 StartZ=0 EndX=31.83 EndY=-28 EndZ=0
    g1: LineSegment StartX=31.83 StartY=-28 StartZ=0 EndX=26.83 EndY=-28 EndZ=0
    g2: LineSegment StartX=26.83 StartY=-28 StartZ=0 EndX=26.83 EndY=-8 EndZ=0
    g3: LineSegment StartX=26.83 StartY=-8 StartZ=0 EndX=29.38 EndY=-8 EndZ=0
    g4: LineSegment StartX=29.38 StartY=-8 StartZ=0 EndX=29.38 EndY=12.5 EndZ=0
    g5: LineSegment StartX=29.38 StartY=12.5 StartZ=0 EndX=31.83 EndY=12.5 EndZ=0
  constraints (18):
    c: Vertical(g0)
    c: Coincident(g0,g1)
    c: Horizontal(g1)
    c: Coincident(g1,g2)
    c: Vertical(g2)
    c: Coincident(g2,g3)
    c: Horizontal(g3)
    c: Coincident(g3,g4)
    c: Coincident(g4,g5)
    c: Coincident(g5,g0)
    c: Horizontal(g5)
    c: DistanceY(g4,g4) = 20.5
    c: DistanceX(g5,g5) = 2.45
    c: DistanceX(g0) = 31.83
    c: DistanceY(g0) = -28
    c: DistanceX(g1,g1) = 5
    c: DistanceY(g4) = 12.5
    c: Vertical(g4)
FEATURE [Sketcher::SketchObject] Sketch479
  ArcFitTolerance = 0
  AttachmentOffset = pos=(0,0,-19) rot=(0,0,1;0rad)
  AttachmentSupport = -> [XZ_Plane294]
  FullyConstrained = true
  MakeInternals = false
  MapMode = 5
  Placement = pos=(0,19,-4.2e-15) rot=(1,0,0;1.5708rad)
  sketch-geometry (6):
    g0: LineSegment StartX=19 StartY=7.5 StartZ=0 EndX=19 EndY=-18 EndZ=0
    g1: LineSegment StartX=19 StartY=-18 StartZ=0 EndX=14 EndY=-18 EndZ=0
    g2: LineSegment StartX=14 StartY=-18 StartZ=0 EndX=14 EndY=-13 EndZ=0
    g3: LineSegment StartX=14 StartY=-13 StartZ=0 EndX=16.55 EndY=-13 EndZ=0
    g4: LineSegment StartX=16.55 StartY=-13 StartZ=0 EndX=16.55 EndY=7.5 EndZ=0
    g5: LineSegment StartX=16.55 StartY=7.5 StartZ=0 EndX=19 EndY=7.5 EndZ=0
  constraints (18):
    c: Vertical(g0)
    c: Coincident(g0,g1)
    c: Horizontal(g1)
    c: Coincident(g1,g2)
    c: Vertical(g2)
    c: Coincident(g2,g3)
    c: Horizontal(g3)
    c: Coincident(g3,g4)
    c: Vertical(g4)
    c: Coincident(g4,g5)
    c: Coincident(g5,g0)
    c: Horizontal(g5)
    c: DistanceX(g5,g5) = 2.45
    c: DistanceX(g0) = 19
    c: DistanceX(g1,g1) = 5
    c: DistanceY(g4,g4) = 20.5
    c: DistanceY(g0) = -18
    c: DistanceY(g2,g2) = 5
FEATURE [Sketcher::SketchObject] Sketch480
  ArcFitTolerance = 0
  AttachmentSupport = -> [XZ_Plane294]
  FullyConstrained = true
  MakeInternals = false
  MapMode = 5
  Placement = pos=(0,0,0) rot=(1,0,0;1.5708rad)
  sketch-geometry (9):
    g0: LineSegment StartX=12 StartY=9 StartZ=0 EndX=13 EndY=9 EndZ=0
    g1: LineSegment StartX=14 StartY=8 StartZ=0 EndX=14 EndY=2 EndZ=0
    g2: LineSegment StartX=13 StartY=1 StartZ=0 EndX=12 EndY=1 EndZ=0
    g3: LineSegment StartX=12 StartY=1 StartZ=0 EndX=12 EndY=9 EndZ=0
    g4: ArcOfCircle CenterX=13 CenterY=8 CenterZ=0 NormalX=0 NormalY=0 NormalZ=1 AngleXU=0 Radius=1 StartAngle=0 EndAngle=1.5708
    g5: GeomPoint [constr] X=14 Y=9 Z=0
    g6: ArcOfCircle CenterX=13 CenterY=2 CenterZ=0 NormalX=0 NormalY=0 NormalZ=1 AngleXU=0 Radius=1 StartAngle=4.71239 EndAngle=6.28319
    g7: GeomPoint [constr] X=14 Y=1 Z=0
    g8: GeomPoint [constr] X=12 Y=5 Z=0
  constraints (21):
    c: Coincident(g2,g3)
    c: Coincident(g3,g0)
    c: Horizontal(g0)
    c: Horizontal(g2)
    c: Vertical(g1)
    c: Vertical(g3)
    c: PointOnObject(g5,g0)
    c: PointOnObject(g5,g1)
    c: Tangent(g0,g4) = 1.5708
    c: Tangent(g1,g4) = 1.5708
    c: PointOnObject(g7,g1)
    c: PointOnObject(g7,g2)
    c: Tangent(g1,g6) = 1.5708
    c: Tangent(g2,g6) = 1.5708
    c: Equal(g4,g6)
    c: Radius(g6) = 1
    c: DistanceY(g3,g3) = 8
    c: DistanceX(g2,g2) = 1
    c: Symmetric(g2,g0,g8)
    c: DistanceY(g8) = 5
    c: DistanceX(g8) = 12
FEATURE [PartDesign::FeatureBase] Clone071
  BaseFeature = -> Body154
  Suppressed = false
FEATURE [PartDesign::Body] Body157  label="mgn9h-carriage-left"
  AllowCompound = false
  Group = -> [Clone071]
  Origin = -> Origin299
  Placement = pos=(0.5,0,10) rot=(0,0,1;0rad)
  Tip = -> Clone071
FEATURE [PartDesign::FeatureBase] Clone
  BaseFeature = -> Body
  Suppressed = false
FEATURE [PartDesign::Pocket] Pocket183
  BaseFeature = -> Clone
  Direction = (0,0,-1)
  Length = 10
  Length2 = 5
  Midplane = true
  Profile = -> Sketch474
  ReferenceAxis = -> Sketch474 [N_Axis]
  Suppressed = false
  Type = 0
FEATURE [PartDesign::Pocket] Pocket184
  BaseFeature = -> Pocket183
  Direction = (0,0,-1)
  Length = 10
  Length2 = 5
  Midplane = true
  Profile = -> Sketch475
  ReferenceAxis = -> Sketch475 [N_Axis]
  Suppressed = false
  Type = 0
FEATURE [PartDesign::Revolution] Revolution
  Angle = 360
  Angle2 = 60
  Axis = (0,2e-16,1)
  Base = (31.83,-19,4.3e-15)
  BaseFeature = -> Pocket184
  Profile = -> Sketch476
  ReferenceAxis = -> Sketch476 [Edge1]
  Reversed = true
  Suppressed = false
  Type = 0
FEATURE [PartDesign::Revolution] Revolution021
  Angle = 360
  Angle2 = 60
  Axis = (0,-2e-16,-1)
  Base = (19,19,-4.4e-15)
  BaseFeature = -> Revolution
  Profile = -> Sketch477
  ReferenceAxis = -> Sketch477 [Edge1]
  Reversed = true
  Suppressed = false
  Type = 0
FEATURE [PartDesign::Groove] Groove012
  Angle = 360
  Angle2 = 60
  Axis = (0,-2e-16,-1)
  Base = (31.83,-19,12.5)
  BaseFeature = -> Revolution021
  Profile = -> Sketch478
  ReferenceAxis = -> Sketch478 [Edge1]
  Suppressed = false
  Type = 0
FEATURE [PartDesign::Groove] Groove013
  Angle = 360
  Angle2 = 60
  Axis = (0,-2e-16,-1)
  Base = (19,19,7.5)
  BaseFeature = -> Groove012
  Profile = -> Sketch479
  ReferenceAxis = -> Sketch479 [Edge1]
  Suppressed = false
  Type = 0
FEATURE [PartDesign::Pocket] Pocket185
  BaseFeature = -> Groove013
  Direction = (0,1,-2e-16)
  Length = 5
  Length2 = 5
  Midplane = true
  Profile = -> Sketch480
  ReferenceAxis = -> Sketch480 [N_Axis]
  Suppressed = false
  Type = 1
FEATURE [PartDesign::Body] Body155  label="y-carriage-rail-left"
  AllowCompound = false
  Group = -> [Clone,Sketch474,Pocket183,Sketch475,Pocket184,Sketch476,Revolution,Sketch477,Revolution021,Sketch478,Groove012,Sketch479,Groove013,Sketch480,Pocket185]
  Origin = -> Origin295
  Tip = -> Pocket185
COMPONENT P6 — recipe-attached ("main-rail-right", modeled in this document).
Construction recipe (the document's own serialized feature program — sketch geometry with constraints, then the solid features built on it; lengths are millimeters unless a unit is written):

FEATURE [Sketcher::SketchObject] Sketch481
  ArcFitTolerance = 0
  AttachmentOffset = pos=(0,0,-5) rot=(0,0,1;0rad)
  AttachmentSupport = -> [XY_Plane297]
  FullyConstrained = true
  MakeInternals = false
  MapMode = 5
  Placement = pos=(0,0,-5) rot=(0,0,1;0rad)
  sketch-geometry (5):
    g0: ArcOfCircle CenterX=31.83 CenterY=-19 CenterZ=0 NormalX=0 NormalY=0 NormalZ=1 AngleXU=0 Radius=9 StartAngle=1.5708 EndAngle=3.14159
    g1: LineSegment StartX=22.83 StartY=-19 StartZ=0 EndX=22.83 EndY=-30 EndZ=0
    g2: LineSegment StartX=22.83 StartY=-30 StartZ=0 EndX=40.83 EndY=-30 EndZ=0
    g3: LineSegment StartX=40.83 StartY=-30 StartZ=0 EndX=40.83 EndY=-10 EndZ=0
    g4: LineSegment StartX=40.83 StartY=-10 StartZ=0 EndX=31.83 EndY=-10 EndZ=0
  constraints (14):
    c: Diameter(g0) = 18
    c: Vertical(g1)
    c: Coincident(g2,g1)
    c: Horizontal(g2)
    c: Coincident(g3,g2)
    c: Vertical(g3)
    c: Coincident(g4,g3)
    c: Horizontal(g4)
    c: Tangent(g0,g1) = -1.5708
    c: Tangent(g0,g4) = -1.5708
    c: Tangent(g3,g0)
    c: DistanceY(g1) = -30
    c: DistanceY(g0) = -19
    c: DistanceX(g0) = 31.83
FEATURE [Sketcher::SketchObject] Sketch482
  ArcFitTolerance = 0
  AttachmentOffset = pos=(0,0,5) rot=(0,0,1;0rad)
  AttachmentSupport = -> [XY_Plane297]
  FullyConstrained = true
  MakeInternals = false
  MapMode = 5
  Placement = pos=(0,0,5) rot=(0,0,1;0rad)
  sketch-geometry (10):
    g0: ArcOfCircle CenterX=19 CenterY=19 CenterZ=0 NormalX=0 NormalY=0 NormalZ=1 AngleXU=0 Radius=9 StartAngle=3.14159 EndAngle=5.25009
    g1: LineSegment StartX=10 StartY=19 StartZ=0 EndX=10 EndY=30 EndZ=0
    g2: LineSegment StartX=10 StartY=30 StartZ=0 EndX=28 EndY=30 EndZ=0
    g3: LineSegment StartX=28 StartY=30 StartZ=0 EndX=28 EndY=19 EndZ=0
    g4: LineSegment StartX=23.6095 StartY=11.27 StartZ=0 EndX=40 EndY=11.27 EndZ=0
    g5: LineSegment StartX=40 StartY=11.27 StartZ=0 EndX=40 EndY=14.65 EndZ=0
    g6: LineSegment StartX=40 StartY=14.65 StartZ=0 EndX=26.8789 EndY=14.65 EndZ=0
    g7: ArcOfCircle CenterX=19 CenterY=19 CenterZ=0 NormalX=0 NormalY=0 NormalZ=1 AngleXU=0 Radius=9 StartAngle=5.77873 EndAngle=6.28319
    g8: GeomPoint [constr] X=19 Y=12.9 Z=0
    g9: Circle [constr] CenterX=19 CenterY=19 CenterZ=0 NormalX=0 NormalY=0 NormalZ=1 AngleXU=0 Radius=6.1
  constraints (27):
    c: Diameter(g0) = 18
    c: Vertical(g1)
    c: Coincident(g2,g1)
    c: Horizontal(g2)
    c: Coincident(g3,g2)
    c: Vertical(g3)
    c: DistanceY(g2) = 30
    c: Tangent(g0,g1) = 1.5708
    c: Horizontal(g4)
    c: Coincident(g5,g4)
    c: Vertical(g5)
    c: Coincident(g6,g5)
    c: Horizontal(g6)
    c: Equal(g0,g7)
    c: Coincident(g0,g4)
    c: Coincident(g7,g6)
    c: Coincident(g0,g7)
    c: Tangent(g7,g3) = 1.5708
    c: DistanceX(g5) = 40
    c: Vertical(g8,g0)
    c: DistanceY(g0,g8) = 1.63
    c: DistanceY(g8,g6) = 1.75
    c: Coincident(g9,g0)
    c: Diameter(g9) = 12.2
    c: PointOnObject(g8,g9)
    c: DistanceX(g0) = 19
    c: DistanceY(g0) = 19
FEATURE [Sketcher::SketchObject] Sketch483
  ArcFitTolerance = 0
  AttachmentOffset = pos=(0,0,19) rot=(0,0,1;0rad)
  AttachmentSupport = -> [XZ_Plane297]
  FullyConstrained = true
  MakeInternals = false
  MapMode = 5
  Placement = pos=(0,-19,4.2e-15) rot=(1,0,0;1.5708rad)
  sketch-geometry (10):
    g0: GeomPoint [constr] X=31.83 Y=-10 Z=0
    g1: GeomPoint [constr] X=31.83 Y=-5 Z=0
    g2: LineSegment StartX=31.83 StartY=-10 StartZ=0 EndX=31.83 EndY=-9.25 EndZ=0
    g3: LineSegment StartX=31.83 StartY=-9.25 StartZ=0 EndX=35.83 EndY=-9.25 EndZ=0
    g4: LineSegment StartX=35.83 StartY=-9.25 StartZ=0 EndX=36.58 EndY=-10 EndZ=0
    g5: LineSegment StartX=36.58 StartY=-10 StartZ=0 EndX=31.83 EndY=-10 EndZ=0
    g6: LineSegment StartX=31.83 StartY=-0.75 StartZ=0 EndX=31.83 EndY=4e-16 EndZ=0
    g7: LineSegment StartX=31.83 StartY=4e-16 StartZ=0 EndX=36.58 EndY=4e-16 EndZ=0
    g8: LineSegment StartX=36.58 StartY=4e-16 StartZ=0 EndX=35.83 EndY=-0.75 EndZ=0
    g9: LineSegment StartX=35.83 StartY=-0.75 StartZ=0 EndX=31.83 EndY=-0.75 EndZ=0
  constraints (26):
    c: Vertical(g1,g0)
    c: Coincident(g2,g0)
    c: Vertical(g2)
    c: Coincident(g2,g3)
    c: Horizontal(g3)
    c: Coincident(g3,g4)
    c: Coincident(g4,g5)
    c: Coincident(g5,g2)
    c: Horizontal(g5)
    c: Coincident(g6,g7)
    c: Horizontal(g7)
    c: Coincident(g7,g8)
    c: Coincident(g8,g9)
    c: Coincident(g9,g6)
    c: Vertical(g6)
    c: Horizontal(g9)
    c: Equal(g2,g6)
    c: DistanceY(g-1,g1) = -5
    c: DistanceX(g1) = 31.83
    c: DistanceX(g3,g3) = 4
    c: Angle(g4) = -0.785398
    c: Perpendicular(g4,g8)
    c: Symmetric(g6,g2,g1)
    c: DistanceY(g2,g6) = 8.5
    c: DistanceY(g2,g6) = 10
    c: Vertical(g8,g3)
FEATURE [Sketcher::SketchObject] Sketch484
  ArcFitTolerance = 0
  AttachmentOffset = pos=(0,0,-19) rot=(0,0,1;0rad)
  AttachmentSupport = -> [XZ_Plane297]
  FullyConstrained = true
  MakeInternals = false
  MapMode = 5
  Placement = pos=(0,19,-4.2e-15) rot=(1,0,0;1.5708rad)
  sketch-geometry (9):
    g0: GeomPoint [constr] X=19 Y=5 Z=0
    g1: LineSegment StartX=19 StartY=10 StartZ=0 EndX=19 EndY=9.25 EndZ=0
    g2: LineSegment StartX=19 StartY=9.25 StartZ=0 EndX=23 EndY=9.25 EndZ=0
    g3: LineSegment StartX=23 StartY=9.25 StartZ=0 EndX=23.75 EndY=10 EndZ=0
    g4: LineSegment StartX=23.75 StartY=10 StartZ=0 EndX=19 EndY=10 EndZ=0
    g5: LineSegment StartX=19 StartY=1e-16 StartZ=0 EndX=19 EndY=0.75 EndZ=0
    g6: LineSegment StartX=19 StartY=0.75 StartZ=0 EndX=23 EndY=0.75 EndZ=0
    g7: LineSegment StartX=23 StartY=0.75 StartZ=0 EndX=23.75 EndY=1e-16 EndZ=0
    g8: LineSegment StartX=23.75 StartY=1e-16 StartZ=0 EndX=19 EndY=1e-16 EndZ=0
  constraints (25):
    c: DistanceX(g0) = 19
    c: DistanceY(g0) = 5
    c: Vertical(g1)
    c: Coincident(g1,g2)
    c: Horizontal(g2)
    c: Coincident(g2,g3)
    c: Coincident(g3,g4)
    c: Coincident(g4,g1)
    c: Horizontal(g4)
    c: Vertical(g5)
    c: Coincident(g5,g6)
    c: Horizontal(g6)
    c: Coincident(g6,g7)
    c: Coincident(g7,g8)
    c: Coincident(g8,g5)
    c: Horizontal(g8)
    c: Symmetric(g5,g1,g0)
    c: Vertical(g5,g1)
    c: Angle(g7) = -0.785398
    c: DistanceX(g6,g6) = 4
    c: Equal(g1,g5)
    c: Perpendicular(g7,g3)
    c: Equal(g2,g6)
    c: DistanceY(g5,g1) = 10
    c: DistanceY(g5,g1) = 8.5
FEATURE [Sketcher::SketchObject] Sketch485
  ArcFitTolerance = 0
  AttachmentOffset = pos=(0,0,-19) rot=(0,0,1;0rad)
  AttachmentSupport = -> [XZ_Plane297]
  FullyConstrained = true
  MakeInternals = false
  MapMode = 5
  Placement = pos=(0,19,-4.2e-15) rot=(1,0,0;1.5708rad)
  sketch-geometry (6):
    g0: LineSegment StartX=19 StartY=12.5 StartZ=0 EndX=19 EndY=-28 EndZ=0
    g1: LineSegment StartX=19 StartY=-28 StartZ=0 EndX=14 EndY=-28 EndZ=0
    g2: LineSegment StartX=14 StartY=-28 StartZ=0 EndX=14 EndY=-8 EndZ=0
    g3: LineSegment StartX=14 StartY=-8 StartZ=0 EndX=16.55 EndY=-8 EndZ=0
    g4: LineSegment StartX=16.55 StartY=-8 StartZ=0 EndX=16.55 EndY=12.5 EndZ=0
    g5: LineSegment StartX=16.55 StartY=12.5 StartZ=0 EndX=19 EndY=12.5 EndZ=0
  constraints (18):
    c: Vertical(g0)
    c: Coincident(g0,g1)
    c: Horizontal(g1)
    c: Coincident(g1,g2)
    c: Vertical(g2)
    c: Coincident(g2,g3)
    c: Horizontal(g3)
    c: Coincident(g3,g4)
    c: Coincident(g4,g5)
    c: Coincident(g5,g0)
    c: Horizontal(g5)
    c: DistanceY(g4,g4) = 20.5
    c: DistanceX(g5,g5) = 2.45
    c: DistanceX(g0) = 19
    c: DistanceY(g0) = -28
    c: DistanceX(g1,g1) = 5
    c: DistanceY(g4) = 12.5
    c: Vertical(g4)
FEATURE [Sketcher::SketchObject] Sketch486
  ArcFitTolerance = 0
  AttachmentOffset = pos=(0,0,19) rot=(0,0,1;0rad)
  AttachmentSupport = -> [XZ_Plane297]
  FullyConstrained = true
  MakeInternals = false
  MapMode = 5
  Placement = pos=(0,-19,4.2e-15) rot=(1,0,0;1.5708rad)
  sketch-geometry (6):
    g0: LineSegment StartX=31.83 StartY=7.5 StartZ=0 EndX=31.83 EndY=-18 EndZ=0
    g1: LineSegment StartX=31.83 StartY=-18 StartZ=0 EndX=26.83 EndY=-18 EndZ=0
    g2: LineSegment StartX=26.83 StartY=-18 StartZ=0 EndX=26.83 EndY=-13 EndZ=0
    g3: LineSegment StartX=26.83 StartY=-13 StartZ=0 EndX=29.38 EndY=-13 EndZ=0
    g4: LineSegment StartX=29.38 StartY=-13 StartZ=0 EndX=29.38 EndY=7.5 EndZ=0
    g5: LineSegment StartX=29.38 StartY=7.5 StartZ=0 EndX=31.83 EndY=7.5 EndZ=0
  constraints (18):
    c: Vertical(g0)
    c: Coincident(g0,g1)
    c: Horizontal(g1)
    c: Coincident(g1,g2)
    c: Vertical(g2)
    c: Coincident(g2,g3)
    c: Horizontal(g3)
    c: Coincident(g3,g4)
    c: Vertical(g4)
    c: Coincident(g4,g5)
    c: Coincident(g5,g0)
    c: Horizontal(g5)
    c: DistanceX(g5,g5) = 2.45
    c: DistanceX(g0) = 31.83
    c: DistanceX(g1,g1) = 5
    c: DistanceY(g4,g4) = 20.5
    c: DistanceY(g0) = -18
    c: DistanceY(g2,g2) = 5
FEATURE [Sketcher::SketchObject] Sketch487
  ArcFitTolerance = 0
  AttachmentSupport = -> [XZ_Plane297]
  FullyConstrained = true
  MakeInternals = false
  MapMode = 5
  Placement = pos=(0,0,0) rot=(1,0,0;1.5708rad)
  sketch-geometry (9):
    g0: LineSegment StartX=12 StartY=-1 StartZ=0 EndX=13 EndY=-1 EndZ=0
    g1: LineSegment StartX=14 StartY=-2 StartZ=0 EndX=14 EndY=-8 EndZ=0
    g2: LineSegment StartX=13 StartY=-9 StartZ=0 EndX=12 EndY=-9 EndZ=0
    g3: LineSegment StartX=12 StartY=-9 StartZ=0 EndX=12 EndY=-1 EndZ=0
    g4: ArcOfCircle CenterX=13 CenterY=-2 CenterZ=0 NormalX=0 NormalY=0 NormalZ=1 AngleXU=0 Radius=1 StartAngle=0 EndAngle=1.5708
    g5: GeomPoint [constr] X=14 Y=-1 Z=0
    g6: ArcOfCircle CenterX=13 CenterY=-8 CenterZ=0 NormalX=0 NormalY=0 NormalZ=1 AngleXU=0 Radius=1 StartAngle=4.71239 EndAngle=6.28319
    g7: GeomPoint [constr] X=14 Y=-9 Z=0
    g8: GeomPoint [constr] X=12 Y=-5 Z=0
  constraints (21):
    c: Coincident(g2,g3)
    c: Coincident(g3,g0)
    c: Horizontal(g0)
    c: Horizontal(g2)
    c: Vertical(g1)
    c: Vertical(g3)
    c: DistanceX(g0,g5) = 2
    c: DistanceY(g3,g3) = 8
    c: PointOnObject(g5,g0)
    c: PointOnObject(g5,g1)
    c: Tangent(g0,g4) = 1.5708
    c: Tangent(g1,g4) = 1.5708
    c: PointOnObject(g7,g1)
    c: PointOnObject(g7,g2)
    c: Tangent(g1,g6) = 1.5708
    c: Tangent(g2,g6) = 1.5708
    c: Equal(g6,g4)
    c: Radius(g4) = 1
    c: Symmetric(g2,g0,g8)
    c: DistanceX(g8) = 12
    c: DistanceY(g8) = -5
FEATURE [PartDesign::FeatureBase] Clone072
  BaseFeature = -> Body154
  Suppressed = false
FEATURE [PartDesign::Body] Body158  label="mgn9h-carriage-right"
  AllowCompound = false
  Group = -> [Clone072]
  Origin = -> Origin300
  Placement = pos=(-0.5,0,10) rot=(0,0,1;0rad)
  Tip = -> Clone072
FEATURE [PartDesign::FeatureBase] Clone070
  BaseFeature = -> Body
  Suppressed = false
FEATURE [PartDesign::Pocket] Pocket186
  BaseFeature = -> Clone070
  Direction = (0,0,-1)
  Length = 10
  Length2 = 5
  Midplane = true
  Profile = -> Sketch481
  ReferenceAxis = -> Sketch481 [N_Axis]
  Suppressed = false
  Type = 0
FEATURE [PartDesign::Pocket] Pocket187
  BaseFeature = -> Pocket186
  Direction = (0,0,-1)
  Length = 10
  Length2 = 5
  Midplane = true
  Profile = -> Sketch482
  ReferenceAxis = -> Sketch482 [N_Axis]
  Suppressed = false
  Type = 0
FEATURE [PartDesign::Revolution] Revolution022
  Angle = 360
  Angle2 = 60
  Axis = (0,2e-16,1)
  Base = (31.83,-19,-0.75)
  BaseFeature = -> Pocket187
  Profile = -> Sketch483
  ReferenceAxis = -> Sketch483 [Edge5]
  Reversed = true
  Suppressed = false
  Type = 0
FEATURE [PartDesign::Revolution] Revolution023
  Angle = 360
  Angle2 = 60
  Axis = (0,-2e-16,-1)
  Base = (19,19,10)
  BaseFeature = -> Revolution022
  Profile = -> Sketch484
  ReferenceAxis = -> Sketch484 [Edge1]
  Reversed = true
  Suppressed = false
  Type = 0
FEATURE [PartDesign::Groove] Groove014
  Angle = 360
  Angle2 = 60
  Axis = (0,-2e-16,-1)
  Base = (19,19,12.5)
  BaseFeature = -> Revolution023
  Profile = -> Sketch485
  ReferenceAxis = -> Sketch485 [Edge1]
  Suppressed = false
  Type = 0
FEATURE [PartDesign::Groove] Groove015
  Angle = 360
  Angle2 = 60
  Axis = (0,-2e-16,-1)
  Base = (31.83,-19,7.5)
  BaseFeature = -> Groove014
  Profile = -> Sketch486
  ReferenceAxis = -> Sketch486 [Edge1]
  Suppressed = false
  Type = 0
FEATURE [PartDesign::Pocket] Pocket188
  BaseFeature = -> Groove015
  Direction = (0,1,-2e-16)
  Length = 5
  Length2 = 5
  Midplane = true
  Profile = -> Sketch487
  ReferenceAxis = -> Sketch487 [N_Axis]
  Suppressed = false
  Type = 1
FEATURE [PartDesign::Body] Body156  label="y-carriage-rail-right-bla"
  AllowCompound = false
  Group = -> [Clone070,Sketch481,Pocket186,Sketch482,Pocket187,Sketch483,Revolution022,Sketch484,Revolution023,Sketch485,Groove014,Sketch486,Groove015,Sketch487,Pocket188]
  Origin = -> Origin298
  Tip = -> Pocket188
PROVENANCE & LICENSES
A FreeCAD (.FCStd) document from a public repository crawl; recipes are the document's own serialized feature recipes (and, for linked parts, companion documents' recipes).
License: as declared in the source repository (recorded in the dataset sidecar).
